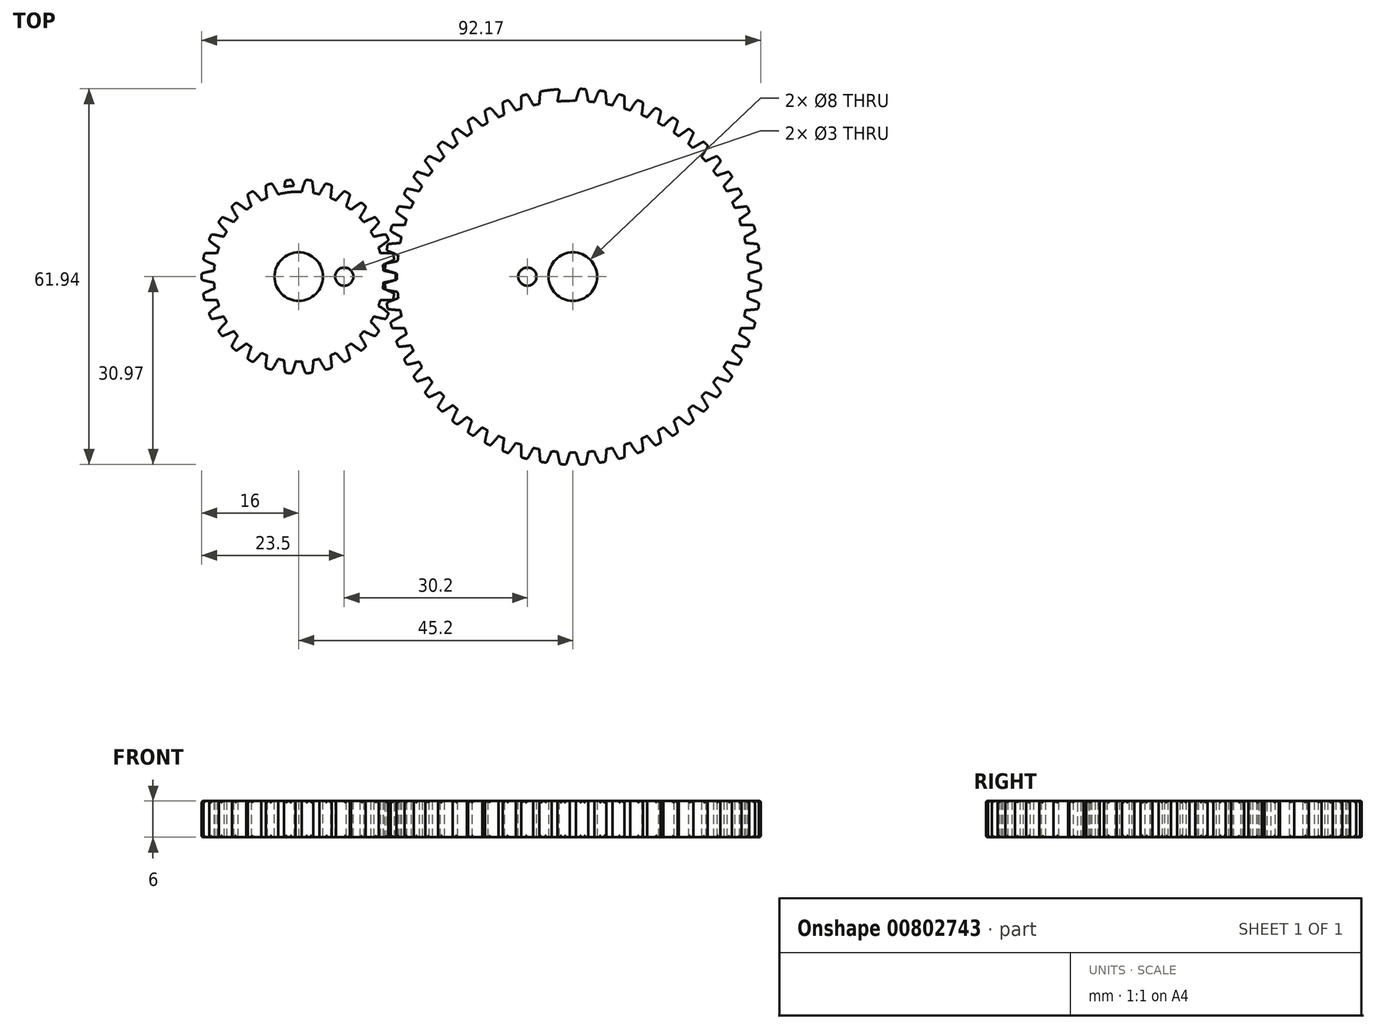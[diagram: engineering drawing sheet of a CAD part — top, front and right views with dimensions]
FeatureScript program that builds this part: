
annotation { "Feature Type Name" : "Feature", "Feature Type Description" : "" }
export const myFeature = defineFeature(function(context is Context, id is Id, definition is map)
    precondition{}
    {
        {
            var Q0;
            Q0=qCreatedBy(makeId("Top.planeOp"),FACE);
            var sketch = newSketch(context, id + "F0", { "sketchPlane" : qUnion([Q0])});
            skCircle(sketch, "E0", {"center": v(0, 0) * mm, "radius": 15 * mm});
            skCircle(sketch, "E1", {"center": v(0, 0) * mm, "radius": 16 * mm});
            skCircle(sketch, "E2", {"center": v(0, 0) * mm, "radius": 14 * mm});
            skLineSegment(sketch, "E3", {"start": v(0, 15) * mm, "end": v(-0.79, 14.98) * mm});
            skLineSegment(sketch, "E4", {"start": v(0, 14) * mm, "end": v(-0.5, 14) * mm});
            skPoint(sketch, "E5.third.point", {"position": v(-19, -4.14) * mm});
            skArc(sketch, "E6.trimOffspring", {"start": v(-0.5, 14) * mm, "mid": v(-0.79, 14.99) * mm, "end": v(-1.14, 15.96) * mm});
            skArc(sketch, "E7.MirrorCS", {"start": v(0.5, 14) * mm, "mid": v(0.79, 14.99) * mm, "end": v(1.14, 15.96) * mm});
            skArc(sketch, "E8.1.0", {"start": v(-3.4, 13.58) * mm, "mid": v(-3.89, 14.5) * mm, "end": v(-4.44, 15.37) * mm});
            skArc(sketch, "E8.1.1", {"start": v(-2.42, 13.79) * mm, "mid": v(-2.35, 14.82) * mm, "end": v(-2.2, 15.85) * mm});
            skArc(sketch, "E8.2.0", {"start": v(-6.15, 12.58) * mm, "mid": v(-6.81, 13.37) * mm, "end": v(-7.54, 14.11) * mm});
            skArc(sketch, "E8.2.1", {"start": v(-5.23, 12.98) * mm, "mid": v(-5.38, 14.01) * mm, "end": v(-5.45, 15.04) * mm});
            skArc(sketch, "E9.1.3.0", {"start": v(-8.63, 11.03) * mm, "mid": v(-9.45, 11.66) * mm, "end": v(-10.3, 12.24) * mm});
            skArc(sketch, "E9.4.3.0", {"start": v(-7.82, 11.61) * mm, "mid": v(-8.17, 12.59) * mm, "end": v(-8.46, 13.58) * mm});
            skArc(sketch, "E9.1.4.0", {"start": v(-10.73, 9) * mm, "mid": v(-11.66, 9.44) * mm, "end": v(-12.62, 9.83) * mm});
            skArc(sketch, "E9.4.4.0", {"start": v(-10.06, 9.73) * mm, "mid": v(-10.61, 10.61) * mm, "end": v(-11.1, 11.53) * mm});
            skArc(sketch, "E9.1.5.0", {"start": v(-12.37, 6.56) * mm, "mid": v(-13.37, 6.81) * mm, "end": v(-14.4, 6.99) * mm});
            skArc(sketch, "E9.4.5.0", {"start": v(-11.87, 7.43) * mm, "mid": v(-12.58, 8.17) * mm, "end": v(-13.25, 8.97) * mm});
            skArc(sketch, "E9.1.6.0", {"start": v(-13.46, 3.85) * mm, "mid": v(-14.5, 3.88) * mm, "end": v(-15.53, 3.84) * mm});
            skArc(sketch, "E9.4.6.0", {"start": v(-13.15, 4.8) * mm, "mid": v(-14, 5.38) * mm, "end": v(-14.82, 6.02) * mm});
            skArc(sketch, "E9.1.7.0", {"start": v(-13.97, 0.97) * mm, "mid": v(-14.99, 0.78) * mm, "end": v(-16, 0.53) * mm});
            skArc(sketch, "E9.4.7.0", {"start": v(-13.86, 1.96) * mm, "mid": v(-14.82, 2.35) * mm, "end": v(-15.75, 2.8) * mm});
            skArc(sketch, "E9.1.8.0", {"start": v(-13.86, -1.96) * mm, "mid": v(-14.82, -2.35) * mm, "end": v(-15.75, -2.8) * mm});
            skArc(sketch, "E9.4.8.0", {"start": v(-13.97, -0.97) * mm, "mid": v(-14.99, -0.78) * mm, "end": v(-16, -0.53) * mm});
            skArc(sketch, "E9.1.9.0", {"start": v(-13.15, -4.8) * mm, "mid": v(-14, -5.38) * mm, "end": v(-14.82, -6.02) * mm});
            skArc(sketch, "E9.4.9.0", {"start": v(-13.46, -3.85) * mm, "mid": v(-14.5, -3.88) * mm, "end": v(-15.53, -3.84) * mm});
            skArc(sketch, "E9.1.10.0", {"start": v(-11.87, -7.43) * mm, "mid": v(-12.58, -8.17) * mm, "end": v(-13.25, -8.97) * mm});
            skArc(sketch, "E9.4.10.0", {"start": v(-12.37, -6.56) * mm, "mid": v(-13.37, -6.81) * mm, "end": v(-14.4, -6.99) * mm});
            skArc(sketch, "E9.1.11.0", {"start": v(-10.06, -9.73) * mm, "mid": v(-10.61, -10.61) * mm, "end": v(-11.1, -11.53) * mm});
            skArc(sketch, "E9.4.11.0", {"start": v(-10.73, -9) * mm, "mid": v(-11.66, -9.44) * mm, "end": v(-12.62, -9.83) * mm});
            skArc(sketch, "E9.1.12.0", {"start": v(-7.82, -11.61) * mm, "mid": v(-8.17, -12.59) * mm, "end": v(-8.46, -13.58) * mm});
            skArc(sketch, "E9.4.12.0", {"start": v(-8.63, -11.03) * mm, "mid": v(-9.45, -11.66) * mm, "end": v(-10.3, -12.24) * mm});
            skArc(sketch, "E9.1.13.0", {"start": v(-5.23, -12.98) * mm, "mid": v(-5.38, -14.01) * mm, "end": v(-5.45, -15.04) * mm});
            skArc(sketch, "E9.4.13.0", {"start": v(-6.15, -12.58) * mm, "mid": v(-6.81, -13.37) * mm, "end": v(-7.54, -14.11) * mm});
            skArc(sketch, "E9.1.14.0", {"start": v(-2.42, -13.79) * mm, "mid": v(-2.35, -14.82) * mm, "end": v(-2.2, -15.85) * mm});
            skArc(sketch, "E9.4.14.0", {"start": v(-3.4, -13.58) * mm, "mid": v(-3.89, -14.5) * mm, "end": v(-4.44, -15.37) * mm});
            skArc(sketch, "E9.1.15.0", {"start": v(0.5, -14) * mm, "mid": v(0.79, -14.99) * mm, "end": v(1.14, -15.96) * mm});
            skArc(sketch, "E9.4.15.0", {"start": v(-0.5, -14) * mm, "mid": v(-0.79, -14.99) * mm, "end": v(-1.14, -15.96) * mm});
            skArc(sketch, "E9.1.16.0", {"start": v(3.4, -13.58) * mm, "mid": v(3.89, -14.5) * mm, "end": v(4.44, -15.37) * mm});
            skArc(sketch, "E9.4.16.0", {"start": v(2.42, -13.79) * mm, "mid": v(2.35, -14.82) * mm, "end": v(2.2, -15.85) * mm});
            skArc(sketch, "E9.1.17.0", {"start": v(6.15, -12.58) * mm, "mid": v(6.81, -13.37) * mm, "end": v(7.54, -14.11) * mm});
            skArc(sketch, "E9.4.17.0", {"start": v(5.23, -12.98) * mm, "mid": v(5.38, -14.01) * mm, "end": v(5.45, -15.04) * mm});
            skArc(sketch, "E9.1.18.0", {"start": v(8.63, -11.03) * mm, "mid": v(9.45, -11.66) * mm, "end": v(10.3, -12.24) * mm});
            skArc(sketch, "E9.4.18.0", {"start": v(7.82, -11.61) * mm, "mid": v(8.17, -12.59) * mm, "end": v(8.46, -13.58) * mm});
            skArc(sketch, "E9.1.19.0", {"start": v(10.73, -9) * mm, "mid": v(11.66, -9.44) * mm, "end": v(12.62, -9.83) * mm});
            skArc(sketch, "E9.4.19.0", {"start": v(10.06, -9.73) * mm, "mid": v(10.61, -10.61) * mm, "end": v(11.1, -11.53) * mm});
            skArc(sketch, "E9.1.20.0", {"start": v(12.37, -6.56) * mm, "mid": v(13.37, -6.81) * mm, "end": v(14.4, -6.99) * mm});
            skArc(sketch, "E9.4.20.0", {"start": v(11.87, -7.43) * mm, "mid": v(12.58, -8.17) * mm, "end": v(13.25, -8.97) * mm});
            skArc(sketch, "E9.1.21.0", {"start": v(13.46, -3.85) * mm, "mid": v(14.5, -3.88) * mm, "end": v(15.53, -3.84) * mm});
            skArc(sketch, "E9.4.21.0", {"start": v(13.15, -4.8) * mm, "mid": v(14, -5.38) * mm, "end": v(14.82, -6.02) * mm});
            skArc(sketch, "E9.1.22.0", {"start": v(13.97, -0.97) * mm, "mid": v(14.99, -0.78) * mm, "end": v(16, -0.53) * mm});
            skArc(sketch, "E9.4.22.0", {"start": v(13.86, -1.96) * mm, "mid": v(14.82, -2.35) * mm, "end": v(15.75, -2.8) * mm});
            skArc(sketch, "E9.1.23.0", {"start": v(13.86, 1.96) * mm, "mid": v(14.82, 2.35) * mm, "end": v(15.75, 2.8) * mm});
            skArc(sketch, "E9.4.23.0", {"start": v(13.97, 0.97) * mm, "mid": v(14.99, 0.78) * mm, "end": v(16, 0.53) * mm});
            skArc(sketch, "E9.1.24.0", {"start": v(13.15, 4.8) * mm, "mid": v(14, 5.38) * mm, "end": v(14.82, 6.02) * mm});
            skArc(sketch, "E9.4.24.0", {"start": v(13.46, 3.85) * mm, "mid": v(14.5, 3.88) * mm, "end": v(15.53, 3.84) * mm});
            skArc(sketch, "E9.1.25.0", {"start": v(11.87, 7.43) * mm, "mid": v(12.58, 8.17) * mm, "end": v(13.25, 8.97) * mm});
            skArc(sketch, "E9.4.25.0", {"start": v(12.37, 6.56) * mm, "mid": v(13.37, 6.81) * mm, "end": v(14.4, 6.99) * mm});
            skArc(sketch, "E9.1.26.0", {"start": v(10.06, 9.73) * mm, "mid": v(10.61, 10.61) * mm, "end": v(11.1, 11.53) * mm});
            skArc(sketch, "E9.4.26.0", {"start": v(10.73, 9) * mm, "mid": v(11.66, 9.44) * mm, "end": v(12.62, 9.83) * mm});
            skArc(sketch, "E9.1.27.0", {"start": v(7.82, 11.61) * mm, "mid": v(8.17, 12.59) * mm, "end": v(8.46, 13.58) * mm});
            skArc(sketch, "E9.4.27.0", {"start": v(8.63, 11.03) * mm, "mid": v(9.45, 11.66) * mm, "end": v(10.3, 12.24) * mm});
            skArc(sketch, "E9.1.28.0", {"start": v(5.23, 12.98) * mm, "mid": v(5.38, 14.01) * mm, "end": v(5.45, 15.04) * mm});
            skArc(sketch, "E9.4.28.0", {"start": v(6.15, 12.58) * mm, "mid": v(6.81, 13.37) * mm, "end": v(7.54, 14.11) * mm});
            skArc(sketch, "E9.1.29.0", {"start": v(2.42, 13.79) * mm, "mid": v(2.35, 14.82) * mm, "end": v(2.2, 15.85) * mm});
            skArc(sketch, "E9.4.29.0", {"start": v(3.4, 13.58) * mm, "mid": v(3.89, 14.5) * mm, "end": v(4.44, 15.37) * mm});
            skSolve(sketch);
        }
        {
            var Q0;
            {var subQ0=sQuery(id+"F0.wireOp",EDGE,"E9.1.14.0");var subQ1=sQuery(id+"F0.wireOp",EDGE,"E0");var subQ2=makeQuery(id+"F0.imprint","INTERSECT",VERTEX,{"derivedFrom":[subQ1,subQ0]});Q0=makeQuery(id+"F0.imprint","IMPRINT",FACE,{"disambiguationData":[TD([[makeQuery(id+"F0.imprint","IMPRINT",EDGE,{"disambiguationData":[TD([[subQ2,-1.0]])],"derivedFrom":subQ1}),-1.0]])]});}
            var Q1;
            {var subQ0=sQuery(id+"F0.wireOp",EDGE,"E9.4.23.0");var subQ1=sQuery(id+"F0.wireOp",EDGE,"E0");var subQ2=makeQuery(id+"F0.imprint","INTERSECT",VERTEX,{"derivedFrom":[subQ1,subQ0]});Q1=makeQuery(id+"F0.imprint","IMPRINT",FACE,{"disambiguationData":[TD([[makeQuery(id+"F0.imprint","IMPRINT",EDGE,{"disambiguationData":[TD([[subQ2,1.0]])],"derivedFrom":subQ1}),-1.0]])]});}
            var Q2;
            {var subQ0=sQuery(id+"F0.wireOp",EDGE,"E9.1.11.0");var subQ1=sQuery(id+"F0.wireOp",EDGE,"E0");var subQ2=makeQuery(id+"F0.imprint","INTERSECT",VERTEX,{"derivedFrom":[subQ1,subQ0]});Q2=makeQuery(id+"F0.imprint","IMPRINT",FACE,{"disambiguationData":[TD([[makeQuery(id+"F0.imprint","IMPRINT",EDGE,{"disambiguationData":[TD([[subQ2,-1.0]])],"derivedFrom":subQ1}),-1.0]])]});}
            var Q3;
            {var subQ0=sQuery(id+"F0.wireOp",EDGE,"E9.1.21.0");var subQ1=sQuery(id+"F0.wireOp",EDGE,"E0");var subQ2=makeQuery(id+"F0.imprint","INTERSECT",VERTEX,{"derivedFrom":[subQ1,subQ0]});Q3=makeQuery(id+"F0.imprint","IMPRINT",FACE,{"disambiguationData":[TD([[makeQuery(id+"F0.imprint","IMPRINT",EDGE,{"disambiguationData":[TD([[subQ2,-1.0]])],"derivedFrom":subQ1}),-1.0]])]});}
            var Q4;
            {var subQ0=sQuery(id+"F0.wireOp",EDGE,"E9.1.10.0");var subQ1=sQuery(id+"F0.wireOp",EDGE,"E0");var subQ2=makeQuery(id+"F0.imprint","INTERSECT",VERTEX,{"derivedFrom":[subQ1,subQ0]});Q4=makeQuery(id+"F0.imprint","IMPRINT",FACE,{"disambiguationData":[TD([[makeQuery(id+"F0.imprint","IMPRINT",EDGE,{"disambiguationData":[TD([[subQ2,-1.0]])],"derivedFrom":subQ1}),-1.0]])]});}
            var Q5;
            {var subQ0=sQuery(id+"F0.wireOp",EDGE,"E9.1.7.0");var subQ1=sQuery(id+"F0.wireOp",EDGE,"E0");var subQ2=makeQuery(id+"F0.imprint","INTERSECT",VERTEX,{"derivedFrom":[subQ1,subQ0]});Q5=makeQuery(id+"F0.imprint","IMPRINT",FACE,{"disambiguationData":[TD([[makeQuery(id+"F0.imprint","IMPRINT",EDGE,{"disambiguationData":[TD([[subQ2,-1.0]])],"derivedFrom":subQ1}),-1.0]])]});}
            var Q6;
            {var subQ0=sQuery(id+"F0.wireOp",EDGE,"E8.1.0");var subQ1=sQuery(id+"F0.wireOp",EDGE,"E0");var subQ2=makeQuery(id+"F0.imprint","INTERSECT",VERTEX,{"derivedFrom":[subQ1,subQ0]});Q6=makeQuery(id+"F0.imprint","IMPRINT",FACE,{"disambiguationData":[TD([[makeQuery(id+"F0.imprint","IMPRINT",EDGE,{"disambiguationData":[TD([[subQ2,-1.0]])],"derivedFrom":subQ1}),-1.0]])]});}
            var Q7;
            {var subQ0=sQuery(id+"F0.wireOp",EDGE,"E9.1.13.0");var subQ1=sQuery(id+"F0.wireOp",EDGE,"E0");var subQ2=makeQuery(id+"F0.imprint","INTERSECT",VERTEX,{"derivedFrom":[subQ1,subQ0]});Q7=makeQuery(id+"F0.imprint","IMPRINT",FACE,{"disambiguationData":[TD([[makeQuery(id+"F0.imprint","IMPRINT",EDGE,{"disambiguationData":[TD([[subQ2,-1.0]])],"derivedFrom":subQ1}),-1.0]])]});}
            var Q8;
            {var subQ0=sQuery(id+"F0.wireOp",EDGE,"E9.1.9.0");var subQ1=sQuery(id+"F0.wireOp",EDGE,"E0");var subQ2=makeQuery(id+"F0.imprint","INTERSECT",VERTEX,{"derivedFrom":[subQ1,subQ0]});Q8=makeQuery(id+"F0.imprint","IMPRINT",FACE,{"disambiguationData":[TD([[makeQuery(id+"F0.imprint","IMPRINT",EDGE,{"disambiguationData":[TD([[subQ2,-1.0]])],"derivedFrom":subQ1}),-1.0]])]});}
            var Q9;
            {var subQ0=sQuery(id+"F0.wireOp",EDGE,"E9.1.18.0");var subQ1=sQuery(id+"F0.wireOp",EDGE,"E0");var subQ2=makeQuery(id+"F0.imprint","INTERSECT",VERTEX,{"derivedFrom":[subQ1,subQ0]});Q9=makeQuery(id+"F0.imprint","IMPRINT",FACE,{"disambiguationData":[TD([[makeQuery(id+"F0.imprint","IMPRINT",EDGE,{"disambiguationData":[TD([[subQ2,-1.0]])],"derivedFrom":subQ1}),-1.0]])]});}
            var Q10;
            {var subQ0=sQuery(id+"F0.wireOp",EDGE,"E9.1.17.0");var subQ1=sQuery(id+"F0.wireOp",EDGE,"E0");var subQ2=makeQuery(id+"F0.imprint","INTERSECT",VERTEX,{"derivedFrom":[subQ1,subQ0]});Q10=makeQuery(id+"F0.imprint","IMPRINT",FACE,{"disambiguationData":[TD([[makeQuery(id+"F0.imprint","IMPRINT",EDGE,{"disambiguationData":[TD([[subQ2,-1.0]])],"derivedFrom":subQ1}),-1.0]])]});}
            var Q11;
            {var subQ0=sQuery(id+"F0.wireOp",EDGE,"E9.1.5.0");var subQ1=sQuery(id+"F0.wireOp",EDGE,"E0");var subQ2=makeQuery(id+"F0.imprint","INTERSECT",VERTEX,{"derivedFrom":[subQ1,subQ0]});Q11=makeQuery(id+"F0.imprint","IMPRINT",FACE,{"disambiguationData":[TD([[makeQuery(id+"F0.imprint","IMPRINT",EDGE,{"disambiguationData":[TD([[subQ2,-1.0]])],"derivedFrom":subQ1}),-1.0]])]});}
            var Q12;
            {var subQ0=sQuery(id+"F0.wireOp",EDGE,"E8.2.0");var subQ1=sQuery(id+"F0.wireOp",EDGE,"E0");var subQ2=makeQuery(id+"F0.imprint","INTERSECT",VERTEX,{"derivedFrom":[subQ1,subQ0]});Q12=makeQuery(id+"F0.imprint","IMPRINT",FACE,{"disambiguationData":[TD([[makeQuery(id+"F0.imprint","IMPRINT",EDGE,{"disambiguationData":[TD([[subQ2,-1.0]])],"derivedFrom":subQ1}),-1.0]])]});}
            var Q13;
            {var subQ0=sQuery(id+"F0.wireOp",EDGE,"E9.1.28.0");var subQ1=sQuery(id+"F0.wireOp",EDGE,"E0");var subQ2=makeQuery(id+"F0.imprint","INTERSECT",VERTEX,{"derivedFrom":[subQ1,subQ0]});Q13=makeQuery(id+"F0.imprint","IMPRINT",FACE,{"disambiguationData":[TD([[makeQuery(id+"F0.imprint","IMPRINT",EDGE,{"disambiguationData":[TD([[subQ2,-1.0]])],"derivedFrom":subQ1}),-1.0]])]});}
            var Q14;
            {var subQ0=sQuery(id+"F0.wireOp",EDGE,"E9.1.29.0");var subQ1=sQuery(id+"F0.wireOp",EDGE,"E0");var subQ2=makeQuery(id+"F0.imprint","INTERSECT",VERTEX,{"derivedFrom":[subQ1,subQ0]});Q14=makeQuery(id+"F0.imprint","IMPRINT",FACE,{"disambiguationData":[TD([[makeQuery(id+"F0.imprint","IMPRINT",EDGE,{"disambiguationData":[TD([[subQ2,-1.0]])],"derivedFrom":subQ1}),-1.0]])]});}
            var Q15;
            {var subQ0=sQuery(id+"F0.wireOp",EDGE,"E9.1.24.0");var subQ1=sQuery(id+"F0.wireOp",EDGE,"E0");var subQ2=makeQuery(id+"F0.imprint","INTERSECT",VERTEX,{"derivedFrom":[subQ1,subQ0]});Q15=makeQuery(id+"F0.imprint","IMPRINT",FACE,{"disambiguationData":[TD([[makeQuery(id+"F0.imprint","IMPRINT",EDGE,{"disambiguationData":[TD([[subQ2,-1.0]])],"derivedFrom":subQ1}),-1.0]])]});}
            var Q16;
            {var subQ0=sQuery(id+"F0.wireOp",EDGE,"E6.trimOffspring");var subQ5=sQuery(id+"F0.wireOp",EDGE,"E1");var subQ6=makeQuery(id+"F0.imprint","INTERSECT",VERTEX,{"derivedFrom":[subQ5,subQ0]});Q16=makeQuery(id+"F0.imprint","IMPRINT",FACE,{"disambiguationData":[TD([[makeQuery(id+"F0.imprint","IMPRINT",EDGE,{"disambiguationData":[TD([[subQ6,-1.0]])],"derivedFrom":subQ5}),1.0]])]});}
            var Q17;
            {var subQ0=sQuery(id+"F0.wireOp",EDGE,"E9.1.27.0");var subQ1=sQuery(id+"F0.wireOp",EDGE,"E0");var subQ2=makeQuery(id+"F0.imprint","INTERSECT",VERTEX,{"derivedFrom":[subQ1,subQ0]});Q17=makeQuery(id+"F0.imprint","IMPRINT",FACE,{"disambiguationData":[TD([[makeQuery(id+"F0.imprint","IMPRINT",EDGE,{"disambiguationData":[TD([[subQ2,-1.0]])],"derivedFrom":subQ1}),-1.0]])]});}
            var Q18;
            {var subQ0=sQuery(id+"F0.wireOp",EDGE,"E9.1.6.0");var subQ1=sQuery(id+"F0.wireOp",EDGE,"E0");var subQ2=makeQuery(id+"F0.imprint","INTERSECT",VERTEX,{"derivedFrom":[subQ1,subQ0]});Q18=makeQuery(id+"F0.imprint","IMPRINT",FACE,{"disambiguationData":[TD([[makeQuery(id+"F0.imprint","IMPRINT",EDGE,{"disambiguationData":[TD([[subQ2,-1.0]])],"derivedFrom":subQ1}),-1.0]])]});}
            var Q19;
            {var subQ0=sQuery(id+"F0.wireOp",EDGE,"E9.1.16.0");var subQ1=sQuery(id+"F0.wireOp",EDGE,"E0");var subQ2=makeQuery(id+"F0.imprint","INTERSECT",VERTEX,{"derivedFrom":[subQ1,subQ0]});Q19=makeQuery(id+"F0.imprint","IMPRINT",FACE,{"disambiguationData":[TD([[makeQuery(id+"F0.imprint","IMPRINT",EDGE,{"disambiguationData":[TD([[subQ2,-1.0]])],"derivedFrom":subQ1}),-1.0]])]});}
            var Q20;
            {var subQ0=sQuery(id+"F0.wireOp",EDGE,"E9.1.12.0");var subQ1=sQuery(id+"F0.wireOp",EDGE,"E0");var subQ2=makeQuery(id+"F0.imprint","INTERSECT",VERTEX,{"derivedFrom":[subQ1,subQ0]});Q20=makeQuery(id+"F0.imprint","IMPRINT",FACE,{"disambiguationData":[TD([[makeQuery(id+"F0.imprint","IMPRINT",EDGE,{"disambiguationData":[TD([[subQ2,-1.0]])],"derivedFrom":subQ1}),-1.0]])]});}
            var Q21;
            {var subQ0=sQuery(id+"F0.wireOp",EDGE,"E9.1.20.0");var subQ1=sQuery(id+"F0.wireOp",EDGE,"E0");var subQ2=makeQuery(id+"F0.imprint","INTERSECT",VERTEX,{"derivedFrom":[subQ1,subQ0]});Q21=makeQuery(id+"F0.imprint","IMPRINT",FACE,{"disambiguationData":[TD([[makeQuery(id+"F0.imprint","IMPRINT",EDGE,{"disambiguationData":[TD([[subQ2,-1.0]])],"derivedFrom":subQ1}),-1.0]])]});}
            var Q22;
            {var subQ0=sQuery(id+"F0.wireOp",EDGE,"E9.1.4.0");var subQ1=sQuery(id+"F0.wireOp",EDGE,"E0");var subQ2=makeQuery(id+"F0.imprint","INTERSECT",VERTEX,{"derivedFrom":[subQ1,subQ0]});Q22=makeQuery(id+"F0.imprint","IMPRINT",FACE,{"disambiguationData":[TD([[makeQuery(id+"F0.imprint","IMPRINT",EDGE,{"disambiguationData":[TD([[subQ2,-1.0]])],"derivedFrom":subQ1}),-1.0]])]});}
            var Q23;
            {var subQ0=sQuery(id+"F0.wireOp",EDGE,"E9.1.15.0");var subQ1=sQuery(id+"F0.wireOp",EDGE,"E0");var subQ2=makeQuery(id+"F0.imprint","INTERSECT",VERTEX,{"derivedFrom":[subQ1,subQ0]});Q23=makeQuery(id+"F0.imprint","IMPRINT",FACE,{"disambiguationData":[TD([[makeQuery(id+"F0.imprint","IMPRINT",EDGE,{"disambiguationData":[TD([[subQ2,-1.0]])],"derivedFrom":subQ1}),-1.0]])]});}
            var Q24;
            {var subQ0=sQuery(id+"F0.wireOp",EDGE,"E9.1.25.0");var subQ1=sQuery(id+"F0.wireOp",EDGE,"E0");var subQ2=makeQuery(id+"F0.imprint","INTERSECT",VERTEX,{"derivedFrom":[subQ1,subQ0]});Q24=makeQuery(id+"F0.imprint","IMPRINT",FACE,{"disambiguationData":[TD([[makeQuery(id+"F0.imprint","IMPRINT",EDGE,{"disambiguationData":[TD([[subQ2,-1.0]])],"derivedFrom":subQ1}),-1.0]])]});}
            var Q25;
            {var subQ0=sQuery(id+"F0.wireOp",EDGE,"E9.1.19.0");var subQ1=sQuery(id+"F0.wireOp",EDGE,"E0");var subQ2=makeQuery(id+"F0.imprint","INTERSECT",VERTEX,{"derivedFrom":[subQ1,subQ0]});Q25=makeQuery(id+"F0.imprint","IMPRINT",FACE,{"disambiguationData":[TD([[makeQuery(id+"F0.imprint","IMPRINT",EDGE,{"disambiguationData":[TD([[subQ2,-1.0]])],"derivedFrom":subQ1}),-1.0]])]});}
            var Q26;
            {var subQ0=sQuery(id+"F0.wireOp",EDGE,"E9.1.26.0");var subQ1=sQuery(id+"F0.wireOp",EDGE,"E0");var subQ2=makeQuery(id+"F0.imprint","INTERSECT",VERTEX,{"derivedFrom":[subQ1,subQ0]});Q26=makeQuery(id+"F0.imprint","IMPRINT",FACE,{"disambiguationData":[TD([[makeQuery(id+"F0.imprint","IMPRINT",EDGE,{"disambiguationData":[TD([[subQ2,-1.0]])],"derivedFrom":subQ1}),-1.0]])]});}
            var Q27;
            {var subQ0=sQuery(id+"F0.wireOp",EDGE,"E9.1.3.0");var subQ1=sQuery(id+"F0.wireOp",EDGE,"E0");var subQ2=makeQuery(id+"F0.imprint","INTERSECT",VERTEX,{"derivedFrom":[subQ1,subQ0]});Q27=makeQuery(id+"F0.imprint","IMPRINT",FACE,{"disambiguationData":[TD([[makeQuery(id+"F0.imprint","IMPRINT",EDGE,{"disambiguationData":[TD([[subQ2,-1.0]])],"derivedFrom":subQ1}),-1.0]])]});}
            var Q28;
            {var subQ0=sQuery(id+"F0.wireOp",EDGE,"E9.1.23.0");var subQ1=sQuery(id+"F0.wireOp",EDGE,"E0");var subQ2=makeQuery(id+"F0.imprint","INTERSECT",VERTEX,{"derivedFrom":[subQ1,subQ0]});Q28=makeQuery(id+"F0.imprint","IMPRINT",FACE,{"disambiguationData":[TD([[makeQuery(id+"F0.imprint","IMPRINT",EDGE,{"disambiguationData":[TD([[subQ2,-1.0]])],"derivedFrom":subQ1}),-1.0]])]});}
            var Q29;
            {var subQ0=sQuery(id+"F0.wireOp",EDGE,"E9.1.8.0");var subQ1=sQuery(id+"F0.wireOp",EDGE,"E0");var subQ2=makeQuery(id+"F0.imprint","INTERSECT",VERTEX,{"derivedFrom":[subQ1,subQ0]});Q29=makeQuery(id+"F0.imprint","IMPRINT",FACE,{"disambiguationData":[TD([[makeQuery(id+"F0.imprint","IMPRINT",EDGE,{"disambiguationData":[TD([[subQ2,-1.0]])],"derivedFrom":subQ1}),-1.0]])]});}
            var Q30;
            {var subQ41=sQuery(id+"F0.wireOp",EDGE,"E4");Q30=makeQuery(id+"F0.imprint","IMPRINT",FACE,{"disambiguationData":[TD([[makeQuery(id+"F0.imprint","IMPRINT",EDGE,{"derivedFrom":subQ41}),1.0]])]});}
            var Q31;
            {var subQ0=sQuery(id+"F0.wireOp",EDGE,"E9.1.27.0");var subQ1=sQuery(id+"F0.wireOp",EDGE,"E0");var subQ2=makeQuery(id+"F0.imprint","INTERSECT",VERTEX,{"derivedFrom":[subQ1,subQ0]});Q31=makeQuery(id+"F0.imprint","IMPRINT",FACE,{"disambiguationData":[TD([[makeQuery(id+"F0.imprint","IMPRINT",EDGE,{"disambiguationData":[TD([[subQ2,-1.0]])],"derivedFrom":subQ1}),1.0]])]});}
            var Q32;
            {var subQ0=sQuery(id+"F0.wireOp",EDGE,"E9.1.28.0");var subQ1=sQuery(id+"F0.wireOp",EDGE,"E0");var subQ2=makeQuery(id+"F0.imprint","INTERSECT",VERTEX,{"derivedFrom":[subQ1,subQ0]});Q32=makeQuery(id+"F0.imprint","IMPRINT",FACE,{"disambiguationData":[TD([[makeQuery(id+"F0.imprint","IMPRINT",EDGE,{"disambiguationData":[TD([[subQ2,-1.0]])],"derivedFrom":subQ1}),1.0]])]});}
            var Q33;
            {var subQ0=sQuery(id+"F0.wireOp",EDGE,"E9.1.26.0");var subQ1=sQuery(id+"F0.wireOp",EDGE,"E0");var subQ2=makeQuery(id+"F0.imprint","INTERSECT",VERTEX,{"derivedFrom":[subQ1,subQ0]});Q33=makeQuery(id+"F0.imprint","IMPRINT",FACE,{"disambiguationData":[TD([[makeQuery(id+"F0.imprint","IMPRINT",EDGE,{"disambiguationData":[TD([[subQ2,-1.0]])],"derivedFrom":subQ1}),1.0]])]});}
            var Q34;
            {var subQ0=sQuery(id+"F0.wireOp",EDGE,"E9.1.25.0");var subQ1=sQuery(id+"F0.wireOp",EDGE,"E0");var subQ2=makeQuery(id+"F0.imprint","INTERSECT",VERTEX,{"derivedFrom":[subQ1,subQ0]});Q34=makeQuery(id+"F0.imprint","IMPRINT",FACE,{"disambiguationData":[TD([[makeQuery(id+"F0.imprint","IMPRINT",EDGE,{"disambiguationData":[TD([[subQ2,-1.0]])],"derivedFrom":subQ1}),1.0]])]});}
            var Q35;
            {var subQ0=sQuery(id+"F0.wireOp",EDGE,"E9.1.24.0");var subQ1=sQuery(id+"F0.wireOp",EDGE,"E0");var subQ2=makeQuery(id+"F0.imprint","INTERSECT",VERTEX,{"derivedFrom":[subQ1,subQ0]});Q35=makeQuery(id+"F0.imprint","IMPRINT",FACE,{"disambiguationData":[TD([[makeQuery(id+"F0.imprint","IMPRINT",EDGE,{"disambiguationData":[TD([[subQ2,-1.0]])],"derivedFrom":subQ1}),1.0]])]});}
            var Q36;
            {var subQ0=sQuery(id+"F0.wireOp",EDGE,"E9.1.23.0");var subQ1=sQuery(id+"F0.wireOp",EDGE,"E0");var subQ2=makeQuery(id+"F0.imprint","INTERSECT",VERTEX,{"derivedFrom":[subQ1,subQ0]});Q36=makeQuery(id+"F0.imprint","IMPRINT",FACE,{"disambiguationData":[TD([[makeQuery(id+"F0.imprint","IMPRINT",EDGE,{"disambiguationData":[TD([[subQ2,-1.0]])],"derivedFrom":subQ1}),1.0]])]});}
            var Q37;
            {var subQ0=sQuery(id+"F0.wireOp",EDGE,"E9.4.23.0");var subQ1=sQuery(id+"F0.wireOp",EDGE,"E0");var subQ2=makeQuery(id+"F0.imprint","INTERSECT",VERTEX,{"derivedFrom":[subQ1,subQ0]});Q37=makeQuery(id+"F0.imprint","IMPRINT",FACE,{"disambiguationData":[TD([[makeQuery(id+"F0.imprint","IMPRINT",EDGE,{"disambiguationData":[TD([[subQ2,1.0]])],"derivedFrom":subQ1}),1.0]])]});}
            var Q38;
            {var subQ0=sQuery(id+"F0.wireOp",EDGE,"E9.1.21.0");var subQ1=sQuery(id+"F0.wireOp",EDGE,"E0");var subQ2=makeQuery(id+"F0.imprint","INTERSECT",VERTEX,{"derivedFrom":[subQ1,subQ0]});Q38=makeQuery(id+"F0.imprint","IMPRINT",FACE,{"disambiguationData":[TD([[makeQuery(id+"F0.imprint","IMPRINT",EDGE,{"disambiguationData":[TD([[subQ2,-1.0]])],"derivedFrom":subQ1}),1.0]])]});}
            var Q39;
            {var subQ0=sQuery(id+"F0.wireOp",EDGE,"E9.1.20.0");var subQ1=sQuery(id+"F0.wireOp",EDGE,"E0");var subQ2=makeQuery(id+"F0.imprint","INTERSECT",VERTEX,{"derivedFrom":[subQ1,subQ0]});Q39=makeQuery(id+"F0.imprint","IMPRINT",FACE,{"disambiguationData":[TD([[makeQuery(id+"F0.imprint","IMPRINT",EDGE,{"disambiguationData":[TD([[subQ2,-1.0]])],"derivedFrom":subQ1}),1.0]])]});}
            var Q40;
            {var subQ0=sQuery(id+"F0.wireOp",EDGE,"E9.1.19.0");var subQ1=sQuery(id+"F0.wireOp",EDGE,"E0");var subQ2=makeQuery(id+"F0.imprint","INTERSECT",VERTEX,{"derivedFrom":[subQ1,subQ0]});Q40=makeQuery(id+"F0.imprint","IMPRINT",FACE,{"disambiguationData":[TD([[makeQuery(id+"F0.imprint","IMPRINT",EDGE,{"disambiguationData":[TD([[subQ2,-1.0]])],"derivedFrom":subQ1}),1.0]])]});}
            var Q41;
            {var subQ0=sQuery(id+"F0.wireOp",EDGE,"E9.1.18.0");var subQ1=sQuery(id+"F0.wireOp",EDGE,"E0");var subQ2=makeQuery(id+"F0.imprint","INTERSECT",VERTEX,{"derivedFrom":[subQ1,subQ0]});Q41=makeQuery(id+"F0.imprint","IMPRINT",FACE,{"disambiguationData":[TD([[makeQuery(id+"F0.imprint","IMPRINT",EDGE,{"disambiguationData":[TD([[subQ2,-1.0]])],"derivedFrom":subQ1}),1.0]])]});}
            var Q42;
            {var subQ0=sQuery(id+"F0.wireOp",EDGE,"E9.1.17.0");var subQ1=sQuery(id+"F0.wireOp",EDGE,"E0");var subQ2=makeQuery(id+"F0.imprint","INTERSECT",VERTEX,{"derivedFrom":[subQ1,subQ0]});Q42=makeQuery(id+"F0.imprint","IMPRINT",FACE,{"disambiguationData":[TD([[makeQuery(id+"F0.imprint","IMPRINT",EDGE,{"disambiguationData":[TD([[subQ2,-1.0]])],"derivedFrom":subQ1}),1.0]])]});}
            var Q43;
            {var subQ0=sQuery(id+"F0.wireOp",EDGE,"E9.1.16.0");var subQ1=sQuery(id+"F0.wireOp",EDGE,"E0");var subQ2=makeQuery(id+"F0.imprint","INTERSECT",VERTEX,{"derivedFrom":[subQ1,subQ0]});Q43=makeQuery(id+"F0.imprint","IMPRINT",FACE,{"disambiguationData":[TD([[makeQuery(id+"F0.imprint","IMPRINT",EDGE,{"disambiguationData":[TD([[subQ2,-1.0]])],"derivedFrom":subQ1}),1.0]])]});}
            var Q44;
            {var subQ0=sQuery(id+"F0.wireOp",EDGE,"E9.1.15.0");var subQ1=sQuery(id+"F0.wireOp",EDGE,"E0");var subQ2=makeQuery(id+"F0.imprint","INTERSECT",VERTEX,{"derivedFrom":[subQ1,subQ0]});Q44=makeQuery(id+"F0.imprint","IMPRINT",FACE,{"disambiguationData":[TD([[makeQuery(id+"F0.imprint","IMPRINT",EDGE,{"disambiguationData":[TD([[subQ2,-1.0]])],"derivedFrom":subQ1}),1.0]])]});}
            var Q45;
            {var subQ0=sQuery(id+"F0.wireOp",EDGE,"E9.1.14.0");var subQ1=sQuery(id+"F0.wireOp",EDGE,"E0");var subQ2=makeQuery(id+"F0.imprint","INTERSECT",VERTEX,{"derivedFrom":[subQ1,subQ0]});Q45=makeQuery(id+"F0.imprint","IMPRINT",FACE,{"disambiguationData":[TD([[makeQuery(id+"F0.imprint","IMPRINT",EDGE,{"disambiguationData":[TD([[subQ2,-1.0]])],"derivedFrom":subQ1}),1.0]])]});}
            var Q46;
            {var subQ0=sQuery(id+"F0.wireOp",EDGE,"E9.1.13.0");var subQ1=sQuery(id+"F0.wireOp",EDGE,"E0");var subQ2=makeQuery(id+"F0.imprint","INTERSECT",VERTEX,{"derivedFrom":[subQ1,subQ0]});Q46=makeQuery(id+"F0.imprint","IMPRINT",FACE,{"disambiguationData":[TD([[makeQuery(id+"F0.imprint","IMPRINT",EDGE,{"disambiguationData":[TD([[subQ2,-1.0]])],"derivedFrom":subQ1}),1.0]])]});}
            var Q47;
            {var subQ0=sQuery(id+"F0.wireOp",EDGE,"E9.1.12.0");var subQ1=sQuery(id+"F0.wireOp",EDGE,"E0");var subQ2=makeQuery(id+"F0.imprint","INTERSECT",VERTEX,{"derivedFrom":[subQ1,subQ0]});Q47=makeQuery(id+"F0.imprint","IMPRINT",FACE,{"disambiguationData":[TD([[makeQuery(id+"F0.imprint","IMPRINT",EDGE,{"disambiguationData":[TD([[subQ2,-1.0]])],"derivedFrom":subQ1}),1.0]])]});}
            var Q48;
            {var subQ0=sQuery(id+"F0.wireOp",EDGE,"E9.1.11.0");var subQ1=sQuery(id+"F0.wireOp",EDGE,"E0");var subQ2=makeQuery(id+"F0.imprint","INTERSECT",VERTEX,{"derivedFrom":[subQ1,subQ0]});Q48=makeQuery(id+"F0.imprint","IMPRINT",FACE,{"disambiguationData":[TD([[makeQuery(id+"F0.imprint","IMPRINT",EDGE,{"disambiguationData":[TD([[subQ2,-1.0]])],"derivedFrom":subQ1}),1.0]])]});}
            var Q49;
            {var subQ0=sQuery(id+"F0.wireOp",EDGE,"E9.1.10.0");var subQ1=sQuery(id+"F0.wireOp",EDGE,"E0");var subQ2=makeQuery(id+"F0.imprint","INTERSECT",VERTEX,{"derivedFrom":[subQ1,subQ0]});Q49=makeQuery(id+"F0.imprint","IMPRINT",FACE,{"disambiguationData":[TD([[makeQuery(id+"F0.imprint","IMPRINT",EDGE,{"disambiguationData":[TD([[subQ2,-1.0]])],"derivedFrom":subQ1}),1.0]])]});}
            var Q50;
            {var subQ0=sQuery(id+"F0.wireOp",EDGE,"E9.1.9.0");var subQ1=sQuery(id+"F0.wireOp",EDGE,"E0");var subQ2=makeQuery(id+"F0.imprint","INTERSECT",VERTEX,{"derivedFrom":[subQ1,subQ0]});Q50=makeQuery(id+"F0.imprint","IMPRINT",FACE,{"disambiguationData":[TD([[makeQuery(id+"F0.imprint","IMPRINT",EDGE,{"disambiguationData":[TD([[subQ2,-1.0]])],"derivedFrom":subQ1}),1.0]])]});}
            var Q51;
            {var subQ0=sQuery(id+"F0.wireOp",EDGE,"E9.1.8.0");var subQ1=sQuery(id+"F0.wireOp",EDGE,"E0");var subQ2=makeQuery(id+"F0.imprint","INTERSECT",VERTEX,{"derivedFrom":[subQ1,subQ0]});Q51=makeQuery(id+"F0.imprint","IMPRINT",FACE,{"disambiguationData":[TD([[makeQuery(id+"F0.imprint","IMPRINT",EDGE,{"disambiguationData":[TD([[subQ2,-1.0]])],"derivedFrom":subQ1}),1.0]])]});}
            var Q52;
            {var subQ0=sQuery(id+"F0.wireOp",EDGE,"E9.1.7.0");var subQ1=sQuery(id+"F0.wireOp",EDGE,"E0");var subQ2=makeQuery(id+"F0.imprint","INTERSECT",VERTEX,{"derivedFrom":[subQ1,subQ0]});Q52=makeQuery(id+"F0.imprint","IMPRINT",FACE,{"disambiguationData":[TD([[makeQuery(id+"F0.imprint","IMPRINT",EDGE,{"disambiguationData":[TD([[subQ2,-1.0]])],"derivedFrom":subQ1}),1.0]])]});}
            var Q53;
            {var subQ0=sQuery(id+"F0.wireOp",EDGE,"E9.1.6.0");var subQ1=sQuery(id+"F0.wireOp",EDGE,"E0");var subQ2=makeQuery(id+"F0.imprint","INTERSECT",VERTEX,{"derivedFrom":[subQ1,subQ0]});Q53=makeQuery(id+"F0.imprint","IMPRINT",FACE,{"disambiguationData":[TD([[makeQuery(id+"F0.imprint","IMPRINT",EDGE,{"disambiguationData":[TD([[subQ2,-1.0]])],"derivedFrom":subQ1}),1.0]])]});}
            var Q54;
            {var subQ0=sQuery(id+"F0.wireOp",EDGE,"E9.1.5.0");var subQ1=sQuery(id+"F0.wireOp",EDGE,"E0");var subQ2=makeQuery(id+"F0.imprint","INTERSECT",VERTEX,{"derivedFrom":[subQ1,subQ0]});Q54=makeQuery(id+"F0.imprint","IMPRINT",FACE,{"disambiguationData":[TD([[makeQuery(id+"F0.imprint","IMPRINT",EDGE,{"disambiguationData":[TD([[subQ2,-1.0]])],"derivedFrom":subQ1}),1.0]])]});}
            var Q55;
            {var subQ0=sQuery(id+"F0.wireOp",EDGE,"E9.1.4.0");var subQ1=sQuery(id+"F0.wireOp",EDGE,"E0");var subQ2=makeQuery(id+"F0.imprint","INTERSECT",VERTEX,{"derivedFrom":[subQ1,subQ0]});Q55=makeQuery(id+"F0.imprint","IMPRINT",FACE,{"disambiguationData":[TD([[makeQuery(id+"F0.imprint","IMPRINT",EDGE,{"disambiguationData":[TD([[subQ2,-1.0]])],"derivedFrom":subQ1}),1.0]])]});}
            var Q56;
            {var subQ0=sQuery(id+"F0.wireOp",EDGE,"E9.1.3.0");var subQ1=sQuery(id+"F0.wireOp",EDGE,"E0");var subQ2=makeQuery(id+"F0.imprint","INTERSECT",VERTEX,{"derivedFrom":[subQ1,subQ0]});Q56=makeQuery(id+"F0.imprint","IMPRINT",FACE,{"disambiguationData":[TD([[makeQuery(id+"F0.imprint","IMPRINT",EDGE,{"disambiguationData":[TD([[subQ2,-1.0]])],"derivedFrom":subQ1}),1.0]])]});}
            var Q57;
            {var subQ0=sQuery(id+"F0.wireOp",EDGE,"E8.2.0");var subQ1=sQuery(id+"F0.wireOp",EDGE,"E0");var subQ2=makeQuery(id+"F0.imprint","INTERSECT",VERTEX,{"derivedFrom":[subQ1,subQ0]});Q57=makeQuery(id+"F0.imprint","IMPRINT",FACE,{"disambiguationData":[TD([[makeQuery(id+"F0.imprint","IMPRINT",EDGE,{"disambiguationData":[TD([[subQ2,-1.0]])],"derivedFrom":subQ1}),1.0]])]});}
            var Q58;
            {var subQ0=sQuery(id+"F0.wireOp",EDGE,"E8.1.0");var subQ1=sQuery(id+"F0.wireOp",EDGE,"E0");var subQ2=makeQuery(id+"F0.imprint","INTERSECT",VERTEX,{"derivedFrom":[subQ1,subQ0]});Q58=makeQuery(id+"F0.imprint","IMPRINT",FACE,{"disambiguationData":[TD([[makeQuery(id+"F0.imprint","IMPRINT",EDGE,{"disambiguationData":[TD([[subQ2,-1.0]])],"derivedFrom":subQ1}),1.0]])]});}
            var Q59;
            {var subQ3=sQuery(id+"F0.wireOp",EDGE,"E8.1.1");var subQ5=sQuery(id+"F0.wireOp",EDGE,"E2");var subQ7=makeQuery(id+"F0.imprint","INTERSECT",VERTEX,{"derivedFrom":[subQ5,subQ3]});Q59=makeQuery(id+"F0.imprint","IMPRINT",FACE,{"disambiguationData":[TD([[makeQuery(id+"F0.imprint","IMPRINT",EDGE,{"disambiguationData":[TD([[subQ7,-1.0]])],"derivedFrom":subQ3}),-1.0]])]});}
            var Q60;
            {var subQ0=sQuery(id+"F0.wireOp",EDGE,"E9.1.29.0");var subQ1=sQuery(id+"F0.wireOp",EDGE,"E0");var subQ2=makeQuery(id+"F0.imprint","INTERSECT",VERTEX,{"derivedFrom":[subQ1,subQ0]});Q60=makeQuery(id+"F0.imprint","IMPRINT",FACE,{"disambiguationData":[TD([[makeQuery(id+"F0.imprint","IMPRINT",EDGE,{"disambiguationData":[TD([[subQ2,-1.0]])],"derivedFrom":subQ1}),1.0]])]});}
            extrude(context, id + "F1", {"entities" : qUnion([Q0, Q1, Q2, Q3, Q4, Q5, Q6, Q7, Q8, Q9, Q10, Q11, Q12, Q13, Q14, Q15, Q16, Q17, Q18, Q19, Q20, Q21, Q22, Q23, Q24, Q25, Q26, Q27, Q28, Q29, Q30, Q31, Q32, Q33, Q34, Q35, Q36, Q37, Q38, Q39, Q40, Q41, Q42, Q43, Q44, Q45, Q46, Q47, Q48, Q49, Q50, Q51, Q52, Q53, Q54, Q55, Q56, Q57, Q58, Q59, Q60]), "depth" : 6 * mm, "offsetDistance" : 25 * mm});
        }
        {
            var Q0;
            Q0=makeQuery(id+"F1.opExtrude","CAP_FACE",FACE,{"disambiguationData":[OSD([sQuery(id+"F0.wireOp",EDGE,"E1"),sQuery(id+"F0.wireOp",EDGE,"E2"),sQuery(id+"F0.wireOp",EDGE,"E4"),sQuery(id+"F0.wireOp",EDGE,"E6.trimOffspring"),sQuery(id+"F0.wireOp",EDGE,"E7.MirrorCS"),sQuery(id+"F0.wireOp",EDGE,"E8.1.0"),sQuery(id+"F0.wireOp",EDGE,"E8.1.1"),sQuery(id+"F0.wireOp",EDGE,"E8.2.0"),sQuery(id+"F0.wireOp",EDGE,"E8.2.1"),sQuery(id+"F0.wireOp",EDGE,"E9.1.3.0"),sQuery(id+"F0.wireOp",EDGE,"E9.4.3.0"),sQuery(id+"F0.wireOp",EDGE,"E9.1.4.0"),sQuery(id+"F0.wireOp",EDGE,"E9.4.4.0"),sQuery(id+"F0.wireOp",EDGE,"E9.1.5.0"),sQuery(id+"F0.wireOp",EDGE,"E9.4.5.0"),sQuery(id+"F0.wireOp",EDGE,"E9.1.6.0"),sQuery(id+"F0.wireOp",EDGE,"E9.4.6.0"),sQuery(id+"F0.wireOp",EDGE,"E9.1.7.0"),sQuery(id+"F0.wireOp",EDGE,"E9.4.7.0"),sQuery(id+"F0.wireOp",EDGE,"E9.1.8.0"),sQuery(id+"F0.wireOp",EDGE,"E9.4.8.0"),sQuery(id+"F0.wireOp",EDGE,"E9.1.9.0"),sQuery(id+"F0.wireOp",EDGE,"E9.4.9.0"),sQuery(id+"F0.wireOp",EDGE,"E9.1.10.0"),sQuery(id+"F0.wireOp",EDGE,"E9.4.10.0"),sQuery(id+"F0.wireOp",EDGE,"E9.1.11.0"),sQuery(id+"F0.wireOp",EDGE,"E9.4.11.0"),sQuery(id+"F0.wireOp",EDGE,"E9.1.12.0"),sQuery(id+"F0.wireOp",EDGE,"E9.4.12.0"),sQuery(id+"F0.wireOp",EDGE,"E9.1.13.0"),sQuery(id+"F0.wireOp",EDGE,"E9.4.13.0"),sQuery(id+"F0.wireOp",EDGE,"E9.1.14.0"),sQuery(id+"F0.wireOp",EDGE,"E9.4.14.0"),sQuery(id+"F0.wireOp",EDGE,"E9.1.15.0"),sQuery(id+"F0.wireOp",EDGE,"E9.4.15.0"),sQuery(id+"F0.wireOp",EDGE,"E9.1.16.0"),sQuery(id+"F0.wireOp",EDGE,"E9.4.16.0"),sQuery(id+"F0.wireOp",EDGE,"E9.1.17.0"),sQuery(id+"F0.wireOp",EDGE,"E9.4.17.0"),sQuery(id+"F0.wireOp",EDGE,"E9.1.18.0"),sQuery(id+"F0.wireOp",EDGE,"E9.4.18.0"),sQuery(id+"F0.wireOp",EDGE,"E9.1.19.0"),sQuery(id+"F0.wireOp",EDGE,"E9.4.19.0"),sQuery(id+"F0.wireOp",EDGE,"E9.1.20.0"),sQuery(id+"F0.wireOp",EDGE,"E9.4.20.0"),sQuery(id+"F0.wireOp",EDGE,"E9.1.21.0"),sQuery(id+"F0.wireOp",EDGE,"E9.4.21.0"),sQuery(id+"F0.wireOp",EDGE,"E9.1.22.0"),sQuery(id+"F0.wireOp",EDGE,"E9.4.22.0"),sQuery(id+"F0.wireOp",EDGE,"E9.1.23.0"),sQuery(id+"F0.wireOp",EDGE,"E9.4.23.0"),sQuery(id+"F0.wireOp",EDGE,"E9.1.24.0"),sQuery(id+"F0.wireOp",EDGE,"E9.4.24.0"),sQuery(id+"F0.wireOp",EDGE,"E9.1.25.0"),sQuery(id+"F0.wireOp",EDGE,"E9.4.25.0"),sQuery(id+"F0.wireOp",EDGE,"E9.1.26.0"),sQuery(id+"F0.wireOp",EDGE,"E9.4.26.0"),sQuery(id+"F0.wireOp",EDGE,"E9.1.27.0"),sQuery(id+"F0.wireOp",EDGE,"E9.4.27.0"),sQuery(id+"F0.wireOp",EDGE,"E9.1.28.0"),sQuery(id+"F0.wireOp",EDGE,"E9.4.28.0"),sQuery(id+"F0.wireOp",EDGE,"E9.1.29.0"),sQuery(id+"F0.wireOp",EDGE,"E9.4.29.0")])],"isStart":false});
            var sketch = newSketch(context, id + "F2", { "sketchPlane" : qUnion([Q0])});
            skCircle(sketch, "E10", {"center": v(0, 0) * mm, "radius": 4 * mm});
            skSolve(sketch);
        }
        {
            var Q0;
            Q0 = qSketchRegion(id + "F2", true);
            extrude(context, id + "F3", {"entities" : qUnion([Q0]), "operationType" : NewBodyOperationType.REMOVE, "endBound" : BoundingType.THROUGH_ALL, "oppositeDirection" : true, "depth" : 25 * mm, "offsetDistance" : 25 * mm});
        }
        {
            var Q0;
            Q0=qCreatedBy(makeId("Top.planeOp"),FACE);
            var sketch = newSketch(context, id + "F4", { "sketchPlane" : qUnion([Q0])});
            skLineSegment(sketch, "E11", {"start": v(0, 0) * mm, "end": v(45.2, 0) * mm});
            skCircle(sketch, "E12", {"center": v(45.2, 0) * mm, "radius": 31 * mm});
            skArc(sketch, "E13", {"start": v(45.99, 29.99) * mm, "mid": v(45.2, 30) * mm, "end": v(44.41, 29.99) * mm});
            skArc(sketch, "E14", {"start": v(45.7, 29) * mm, "mid": v(45.2, 29) * mm, "end": v(44.7, 29) * mm});
            skLineSegment(sketch, "E15", {"start": v(45.2, 0) * mm, "end": v(45.2, 46.66) * mm});
            skLineSegment(sketch, "E16", {"start": v(45.2, 30) * mm, "end": v(44.41, 29.99) * mm});
            skLineSegment(sketch, "E17", {"start": v(45.2, 29) * mm, "end": v(44.7, 29) * mm});
            skPoint(sketch, "E18.third.point", {"position": v(13.43, -8.7) * mm});
            skArc(sketch, "E19.trimOffspring", {"start": v(44.7, 29) * mm, "mid": v(44.41, 30) * mm, "end": v(44.1, 30.98) * mm});
            skArc(sketch, "E20.MirrorCS", {"start": v(45.7, 29) * mm, "mid": v(45.99, 30) * mm, "end": v(46.3, 30.98) * mm});
            skArc(sketch, "E21.1.0", {"start": v(42.67, 28.89) * mm, "mid": v(42.85, 29.91) * mm, "end": v(43.06, 30.93) * mm});
            skArc(sketch, "E21.1.1", {"start": v(41.67, 28.78) * mm, "mid": v(41.28, 29.75) * mm, "end": v(40.86, 30.7) * mm});
            skArc(sketch, "E21.2.0", {"start": v(39.66, 28.47) * mm, "mid": v(39.73, 29.5) * mm, "end": v(39.84, 30.53) * mm});
            skArc(sketch, "E21.2.1", {"start": v(38.68, 28.26) * mm, "mid": v(38.2, 29.17) * mm, "end": v(37.68, 30.07) * mm});
            skArc(sketch, "E21.3.0", {"start": v(36.72, 27.73) * mm, "mid": v(36.68, 28.77) * mm, "end": v(36.68, 29.8) * mm});
            skArc(sketch, "E21.3.1", {"start": v(35.76, 27.42) * mm, "mid": v(35.18, 28.28) * mm, "end": v(34.57, 29.12) * mm});
            skArc(sketch, "E21.4.0", {"start": v(33.86, 26.7) * mm, "mid": v(33.72, 27.72) * mm, "end": v(33.61, 28.75) * mm});
            skArc(sketch, "E21.4.1", {"start": v(32.95, 26.29) * mm, "mid": v(32.28, 27.08) * mm, "end": v(31.59, 27.85) * mm});
            skArc(sketch, "E21.5.0", {"start": v(31.14, 25.36) * mm, "mid": v(30.88, 26.37) * mm, "end": v(30.67, 27.38) * mm});
            skArc(sketch, "E21.5.1", {"start": v(30.27, 24.86) * mm, "mid": v(29.52, 25.58) * mm, "end": v(28.75, 26.28) * mm});
            skArc(sketch, "E21.6.0", {"start": v(28.56, 23.75) * mm, "mid": v(28.2, 24.73) * mm, "end": v(27.89, 25.71) * mm});
            skArc(sketch, "E21.6.1", {"start": v(27.75, 23.16) * mm, "mid": v(26.93, 23.8) * mm, "end": v(26.1, 24.41) * mm});
            skArc(sketch, "E21.7.0", {"start": v(26.17, 21.88) * mm, "mid": v(25.72, 22.82) * mm, "end": v(25.3, 23.76) * mm});
            skArc(sketch, "E21.7.1", {"start": v(25.43, 21.21) * mm, "mid": v(24.55, 21.76) * mm, "end": v(23.65, 22.28) * mm});
            skArc(sketch, "E21.8.0", {"start": v(23.99, 19.77) * mm, "mid": v(23.44, 20.65) * mm, "end": v(22.92, 21.55) * mm});
            skArc(sketch, "E21.8.1", {"start": v(23.32, 19.03) * mm, "mid": v(22.38, 19.48) * mm, "end": v(21.44, 19.9) * mm});
            skArc(sketch, "E21.9.0", {"start": v(22.04, 17.45) * mm, "mid": v(21.4, 18.27) * mm, "end": v(20.79, 19.1) * mm});
            skArc(sketch, "E21.9.1", {"start": v(21.45, 16.64) * mm, "mid": v(20.47, 17) * mm, "end": v(19.49, 17.31) * mm});
            skArc(sketch, "E21.10.0", {"start": v(20.34, 14.93) * mm, "mid": v(19.62, 15.68) * mm, "end": v(18.92, 16.45) * mm});
            skArc(sketch, "E21.10.1", {"start": v(19.84, 14.06) * mm, "mid": v(18.83, 14.32) * mm, "end": v(17.82, 14.53) * mm});
            skArc(sketch, "E21.11.0", {"start": v(18.91, 12.25) * mm, "mid": v(18.12, 12.92) * mm, "end": v(17.35, 13.61) * mm});
            skArc(sketch, "E21.11.1", {"start": v(18.5, 11.34) * mm, "mid": v(17.48, 11.48) * mm, "end": v(16.45, 11.59) * mm});
            skArc(sketch, "E21.12.0", {"start": v(17.78, 9.44) * mm, "mid": v(16.92, 10.02) * mm, "end": v(16.08, 10.63) * mm});
            skArc(sketch, "E21.12.1", {"start": v(17.47, 8.48) * mm, "mid": v(16.43, 8.52) * mm, "end": v(15.4, 8.52) * mm});
            skArc(sketch, "E21.13.0", {"start": v(16.94, 6.52) * mm, "mid": v(16.03, 7) * mm, "end": v(15.13, 7.52) * mm});
            skArc(sketch, "E21.13.1", {"start": v(16.73, 5.54) * mm, "mid": v(15.7, 5.47) * mm, "end": v(14.67, 5.36) * mm});
            skArc(sketch, "E21.14.0", {"start": v(16.42, 3.53) * mm, "mid": v(15.45, 3.92) * mm, "end": v(14.5, 4.34) * mm});
            skArc(sketch, "E21.14.1", {"start": v(16.31, 2.53) * mm, "mid": v(15.29, 2.35) * mm, "end": v(14.27, 2.14) * mm});
            skArc(sketch, "E21.15.0", {"start": v(16.2, 0.5) * mm, "mid": v(15.2, 0.79) * mm, "end": v(14.22, 1.1) * mm});
            skArc(sketch, "E21.15.1", {"start": v(16.2, -0.5) * mm, "mid": v(15.2, -0.79) * mm, "end": v(14.22, -1.1) * mm});
            skArc(sketch, "E21.16.0", {"start": v(16.31, -2.53) * mm, "mid": v(15.29, -2.35) * mm, "end": v(14.27, -2.14) * mm});
            skArc(sketch, "E21.16.1", {"start": v(16.42, -3.53) * mm, "mid": v(15.45, -3.92) * mm, "end": v(14.5, -4.34) * mm});
            skArc(sketch, "E21.17.0", {"start": v(16.73, -5.54) * mm, "mid": v(15.7, -5.47) * mm, "end": v(14.67, -5.36) * mm});
            skArc(sketch, "E21.17.1", {"start": v(16.94, -6.52) * mm, "mid": v(16.03, -7) * mm, "end": v(15.13, -7.52) * mm});
            skArc(sketch, "E21.18.0", {"start": v(17.47, -8.48) * mm, "mid": v(16.43, -8.52) * mm, "end": v(15.4, -8.52) * mm});
            skArc(sketch, "E21.18.1", {"start": v(17.78, -9.44) * mm, "mid": v(16.92, -10.02) * mm, "end": v(16.08, -10.63) * mm});
            skArc(sketch, "E21.19.0", {"start": v(18.5, -11.34) * mm, "mid": v(17.48, -11.48) * mm, "end": v(16.45, -11.59) * mm});
            skArc(sketch, "E21.19.1", {"start": v(18.91, -12.25) * mm, "mid": v(18.12, -12.92) * mm, "end": v(17.35, -13.61) * mm});
            skArc(sketch, "E21.20.0", {"start": v(19.84, -14.06) * mm, "mid": v(18.83, -14.32) * mm, "end": v(17.82, -14.53) * mm});
            skArc(sketch, "E21.20.1", {"start": v(20.34, -14.93) * mm, "mid": v(19.62, -15.68) * mm, "end": v(18.92, -16.45) * mm});
            skArc(sketch, "E21.21.0", {"start": v(21.45, -16.64) * mm, "mid": v(20.47, -17) * mm, "end": v(19.49, -17.31) * mm});
            skArc(sketch, "E21.21.1", {"start": v(22.04, -17.45) * mm, "mid": v(21.4, -18.27) * mm, "end": v(20.79, -19.1) * mm});
            skArc(sketch, "E21.22.0", {"start": v(23.32, -19.03) * mm, "mid": v(22.38, -19.48) * mm, "end": v(21.44, -19.9) * mm});
            skArc(sketch, "E21.22.1", {"start": v(23.99, -19.77) * mm, "mid": v(23.44, -20.65) * mm, "end": v(22.92, -21.55) * mm});
            skArc(sketch, "E21.23.0", {"start": v(25.43, -21.21) * mm, "mid": v(24.55, -21.76) * mm, "end": v(23.65, -22.28) * mm});
            skArc(sketch, "E21.23.1", {"start": v(26.17, -21.88) * mm, "mid": v(25.72, -22.82) * mm, "end": v(25.3, -23.76) * mm});
            skArc(sketch, "E21.24.0", {"start": v(27.75, -23.16) * mm, "mid": v(26.93, -23.8) * mm, "end": v(26.1, -24.41) * mm});
            skArc(sketch, "E21.24.1", {"start": v(28.56, -23.75) * mm, "mid": v(28.2, -24.73) * mm, "end": v(27.89, -25.71) * mm});
            skArc(sketch, "E21.25.0", {"start": v(30.27, -24.86) * mm, "mid": v(29.52, -25.58) * mm, "end": v(28.75, -26.28) * mm});
            skArc(sketch, "E21.25.1", {"start": v(31.14, -25.36) * mm, "mid": v(30.88, -26.37) * mm, "end": v(30.67, -27.38) * mm});
            skArc(sketch, "E21.26.0", {"start": v(32.95, -26.29) * mm, "mid": v(32.28, -27.08) * mm, "end": v(31.59, -27.85) * mm});
            skArc(sketch, "E21.26.1", {"start": v(33.86, -26.7) * mm, "mid": v(33.72, -27.72) * mm, "end": v(33.61, -28.75) * mm});
            skArc(sketch, "E21.27.0", {"start": v(35.76, -27.42) * mm, "mid": v(35.18, -28.28) * mm, "end": v(34.57, -29.12) * mm});
            skArc(sketch, "E21.27.1", {"start": v(36.72, -27.73) * mm, "mid": v(36.68, -28.77) * mm, "end": v(36.68, -29.8) * mm});
            skArc(sketch, "E21.28.0", {"start": v(38.68, -28.26) * mm, "mid": v(38.2, -29.17) * mm, "end": v(37.68, -30.07) * mm});
            skArc(sketch, "E21.28.1", {"start": v(39.66, -28.47) * mm, "mid": v(39.73, -29.5) * mm, "end": v(39.84, -30.53) * mm});
            skArc(sketch, "E21.29.0", {"start": v(41.67, -28.78) * mm, "mid": v(41.28, -29.75) * mm, "end": v(40.86, -30.7) * mm});
            skArc(sketch, "E21.29.1", {"start": v(42.67, -28.89) * mm, "mid": v(42.85, -29.91) * mm, "end": v(43.06, -30.93) * mm});
            skArc(sketch, "E21.30.0", {"start": v(44.7, -29) * mm, "mid": v(44.41, -30) * mm, "end": v(44.1, -30.98) * mm});
            skArc(sketch, "E21.30.1", {"start": v(45.7, -29) * mm, "mid": v(45.99, -30) * mm, "end": v(46.3, -30.98) * mm});
            skArc(sketch, "E21.31.0", {"start": v(47.73, -28.89) * mm, "mid": v(47.55, -29.91) * mm, "end": v(47.34, -30.93) * mm});
            skArc(sketch, "E21.31.1", {"start": v(48.73, -28.78) * mm, "mid": v(49.12, -29.75) * mm, "end": v(49.54, -30.7) * mm});
            skArc(sketch, "E21.32.0", {"start": v(50.74, -28.47) * mm, "mid": v(50.67, -29.5) * mm, "end": v(50.56, -30.53) * mm});
            skArc(sketch, "E21.32.1", {"start": v(51.72, -28.26) * mm, "mid": v(52.2, -29.17) * mm, "end": v(52.72, -30.07) * mm});
            skArc(sketch, "E21.33.0", {"start": v(53.68, -27.73) * mm, "mid": v(53.72, -28.77) * mm, "end": v(53.72, -29.8) * mm});
            skArc(sketch, "E21.33.1", {"start": v(54.64, -27.42) * mm, "mid": v(55.22, -28.28) * mm, "end": v(55.83, -29.12) * mm});
            skArc(sketch, "E21.34.0", {"start": v(56.54, -26.7) * mm, "mid": v(56.68, -27.72) * mm, "end": v(56.79, -28.75) * mm});
            skArc(sketch, "E21.34.1", {"start": v(57.45, -26.29) * mm, "mid": v(58.12, -27.08) * mm, "end": v(58.81, -27.85) * mm});
            skArc(sketch, "E21.35.0", {"start": v(59.26, -25.36) * mm, "mid": v(59.52, -26.37) * mm, "end": v(59.73, -27.38) * mm});
            skArc(sketch, "E21.35.1", {"start": v(60.13, -24.86) * mm, "mid": v(60.88, -25.58) * mm, "end": v(61.65, -26.28) * mm});
            skArc(sketch, "E21.36.0", {"start": v(61.84, -23.75) * mm, "mid": v(62.2, -24.73) * mm, "end": v(62.51, -25.71) * mm});
            skArc(sketch, "E21.36.1", {"start": v(62.65, -23.16) * mm, "mid": v(63.47, -23.8) * mm, "end": v(64.3, -24.41) * mm});
            skArc(sketch, "E21.37.0", {"start": v(64.23, -21.88) * mm, "mid": v(64.68, -22.82) * mm, "end": v(65.1, -23.76) * mm});
            skArc(sketch, "E21.37.1", {"start": v(64.97, -21.21) * mm, "mid": v(65.85, -21.76) * mm, "end": v(66.75, -22.28) * mm});
            skArc(sketch, "E21.38.0", {"start": v(66.41, -19.77) * mm, "mid": v(66.96, -20.65) * mm, "end": v(67.48, -21.55) * mm});
            skArc(sketch, "E21.38.1", {"start": v(67.08, -19.03) * mm, "mid": v(68.02, -19.48) * mm, "end": v(68.96, -19.9) * mm});
            skArc(sketch, "E21.39.0", {"start": v(68.36, -17.45) * mm, "mid": v(69, -18.27) * mm, "end": v(69.61, -19.1) * mm});
            skArc(sketch, "E21.39.1", {"start": v(68.95, -16.64) * mm, "mid": v(69.93, -17) * mm, "end": v(70.91, -17.31) * mm});
            skArc(sketch, "E21.40.0", {"start": v(70.06, -14.93) * mm, "mid": v(70.78, -15.68) * mm, "end": v(71.48, -16.45) * mm});
            skArc(sketch, "E21.40.1", {"start": v(70.56, -14.06) * mm, "mid": v(71.57, -14.32) * mm, "end": v(72.58, -14.53) * mm});
            skArc(sketch, "E21.41.0", {"start": v(71.49, -12.25) * mm, "mid": v(72.28, -12.92) * mm, "end": v(73.05, -13.61) * mm});
            skArc(sketch, "E21.41.1", {"start": v(71.9, -11.34) * mm, "mid": v(72.92, -11.48) * mm, "end": v(73.95, -11.59) * mm});
            skArc(sketch, "E21.42.0", {"start": v(72.62, -9.44) * mm, "mid": v(73.48, -10.02) * mm, "end": v(74.32, -10.63) * mm});
            skArc(sketch, "E21.42.1", {"start": v(72.93, -8.48) * mm, "mid": v(73.97, -8.52) * mm, "end": v(75, -8.52) * mm});
            skArc(sketch, "E21.43.0", {"start": v(73.46, -6.52) * mm, "mid": v(74.37, -7) * mm, "end": v(75.27, -7.52) * mm});
            skArc(sketch, "E21.43.1", {"start": v(73.67, -5.54) * mm, "mid": v(74.7, -5.47) * mm, "end": v(75.73, -5.36) * mm});
            skArc(sketch, "E21.44.0", {"start": v(73.98, -3.53) * mm, "mid": v(74.95, -3.92) * mm, "end": v(75.9, -4.34) * mm});
            skArc(sketch, "E21.44.1", {"start": v(74.09, -2.53) * mm, "mid": v(75.11, -2.35) * mm, "end": v(76.13, -2.14) * mm});
            skArc(sketch, "E21.45.0", {"start": v(74.2, -0.5) * mm, "mid": v(75.2, -0.79) * mm, "end": v(76.18, -1.1) * mm});
            skArc(sketch, "E21.45.1", {"start": v(74.2, 0.5) * mm, "mid": v(75.2, 0.79) * mm, "end": v(76.18, 1.1) * mm});
            skArc(sketch, "E21.46.0", {"start": v(74.09, 2.53) * mm, "mid": v(75.11, 2.35) * mm, "end": v(76.13, 2.14) * mm});
            skArc(sketch, "E21.46.1", {"start": v(73.98, 3.53) * mm, "mid": v(74.95, 3.92) * mm, "end": v(75.9, 4.34) * mm});
            skArc(sketch, "E21.47.0", {"start": v(73.67, 5.54) * mm, "mid": v(74.7, 5.47) * mm, "end": v(75.73, 5.36) * mm});
            skArc(sketch, "E21.47.1", {"start": v(73.46, 6.52) * mm, "mid": v(74.37, 7) * mm, "end": v(75.27, 7.52) * mm});
            skArc(sketch, "E21.48.0", {"start": v(72.93, 8.48) * mm, "mid": v(73.97, 8.52) * mm, "end": v(75, 8.52) * mm});
            skArc(sketch, "E21.48.1", {"start": v(72.62, 9.44) * mm, "mid": v(73.48, 10.02) * mm, "end": v(74.32, 10.63) * mm});
            skArc(sketch, "E21.49.0", {"start": v(71.9, 11.34) * mm, "mid": v(72.92, 11.48) * mm, "end": v(73.95, 11.59) * mm});
            skArc(sketch, "E21.49.1", {"start": v(71.49, 12.25) * mm, "mid": v(72.28, 12.92) * mm, "end": v(73.05, 13.61) * mm});
            skArc(sketch, "E21.50.0", {"start": v(70.56, 14.06) * mm, "mid": v(71.57, 14.32) * mm, "end": v(72.58, 14.53) * mm});
            skArc(sketch, "E21.50.1", {"start": v(70.06, 14.93) * mm, "mid": v(70.78, 15.68) * mm, "end": v(71.48, 16.45) * mm});
            skArc(sketch, "E21.51.0", {"start": v(68.95, 16.64) * mm, "mid": v(69.93, 17) * mm, "end": v(70.91, 17.31) * mm});
            skArc(sketch, "E21.51.1", {"start": v(68.36, 17.45) * mm, "mid": v(69, 18.27) * mm, "end": v(69.61, 19.1) * mm});
            skArc(sketch, "E21.52.0", {"start": v(67.08, 19.03) * mm, "mid": v(68.02, 19.48) * mm, "end": v(68.96, 19.9) * mm});
            skArc(sketch, "E21.52.1", {"start": v(66.41, 19.77) * mm, "mid": v(66.96, 20.65) * mm, "end": v(67.48, 21.55) * mm});
            skArc(sketch, "E21.53.0", {"start": v(64.97, 21.21) * mm, "mid": v(65.85, 21.76) * mm, "end": v(66.75, 22.28) * mm});
            skArc(sketch, "E21.53.1", {"start": v(64.23, 21.88) * mm, "mid": v(64.68, 22.82) * mm, "end": v(65.1, 23.76) * mm});
            skArc(sketch, "E21.54.0", {"start": v(62.65, 23.16) * mm, "mid": v(63.47, 23.8) * mm, "end": v(64.3, 24.41) * mm});
            skArc(sketch, "E21.54.1", {"start": v(61.84, 23.75) * mm, "mid": v(62.2, 24.73) * mm, "end": v(62.51, 25.71) * mm});
            skArc(sketch, "E21.55.0", {"start": v(60.13, 24.86) * mm, "mid": v(60.88, 25.58) * mm, "end": v(61.65, 26.28) * mm});
            skArc(sketch, "E21.55.1", {"start": v(59.26, 25.36) * mm, "mid": v(59.52, 26.37) * mm, "end": v(59.73, 27.38) * mm});
            skArc(sketch, "E21.56.0", {"start": v(57.45, 26.29) * mm, "mid": v(58.12, 27.08) * mm, "end": v(58.81, 27.85) * mm});
            skArc(sketch, "E21.56.1", {"start": v(56.54, 26.7) * mm, "mid": v(56.68, 27.72) * mm, "end": v(56.79, 28.75) * mm});
            skArc(sketch, "E21.57.0", {"start": v(54.64, 27.42) * mm, "mid": v(55.22, 28.28) * mm, "end": v(55.83, 29.12) * mm});
            skArc(sketch, "E21.57.1", {"start": v(53.68, 27.73) * mm, "mid": v(53.72, 28.77) * mm, "end": v(53.72, 29.8) * mm});
            skArc(sketch, "E21.58.0", {"start": v(51.72, 28.26) * mm, "mid": v(52.2, 29.17) * mm, "end": v(52.72, 30.07) * mm});
            skArc(sketch, "E21.58.1", {"start": v(50.74, 28.47) * mm, "mid": v(50.67, 29.5) * mm, "end": v(50.56, 30.53) * mm});
            skArc(sketch, "E21.59.0", {"start": v(48.73, 28.78) * mm, "mid": v(49.12, 29.75) * mm, "end": v(49.54, 30.7) * mm});
            skArc(sketch, "E21.59.1", {"start": v(47.73, 28.89) * mm, "mid": v(47.55, 29.91) * mm, "end": v(47.34, 30.93) * mm});
            skCircle(sketch, "E22", {"center": v(45.2, 0) * mm, "radius": 29 * mm});
            skSolve(sketch);
        }
        {
            var Q0;
            {var subQ0=sQuery(id+"F4.wireOp",EDGE,"E21.30.1");Q0=makeQuery(id+"F4.imprint","IMPRINT",FACE,{"disambiguationData":[TD([[makeQuery(id+"F4.imprint","IMPRINT",EDGE,{"derivedFrom":subQ0}),1.0]])]});}
            var Q1;
            {var subQ0=sQuery(id+"F4.wireOp",EDGE,"E21.26.1");Q1=makeQuery(id+"F4.imprint","IMPRINT",FACE,{"disambiguationData":[TD([[makeQuery(id+"F4.imprint","IMPRINT",EDGE,{"derivedFrom":subQ0}),1.0]])]});}
            var Q2;
            {var subQ13=sQuery(id+"F4.wireOp",EDGE,"E17");Q2=makeQuery(id+"F4.imprint","IMPRINT",FACE,{"disambiguationData":[TD([[makeQuery(id+"F4.imprint","IMPRINT",EDGE,{"derivedFrom":subQ13}),1.0]])]});}
            var Q3;
            {var subQ0=sQuery(id+"F4.wireOp",EDGE,"E21.40.1");Q3=makeQuery(id+"F4.imprint","IMPRINT",FACE,{"disambiguationData":[TD([[makeQuery(id+"F4.imprint","IMPRINT",EDGE,{"derivedFrom":subQ0}),1.0]])]});}
            var Q4;
            {var subQ0=sQuery(id+"F4.wireOp",EDGE,"E21.10.1");Q4=makeQuery(id+"F4.imprint","IMPRINT",FACE,{"disambiguationData":[TD([[makeQuery(id+"F4.imprint","IMPRINT",EDGE,{"derivedFrom":subQ0}),1.0]])]});}
            var Q5;
            {var subQ0=sQuery(id+"F4.wireOp",EDGE,"E21.54.1");Q5=makeQuery(id+"F4.imprint","IMPRINT",FACE,{"disambiguationData":[TD([[makeQuery(id+"F4.imprint","IMPRINT",EDGE,{"derivedFrom":subQ0}),1.0]])]});}
            var Q6;
            {var subQ0=sQuery(id+"F4.wireOp",EDGE,"E21.14.1");Q6=makeQuery(id+"F4.imprint","IMPRINT",FACE,{"disambiguationData":[TD([[makeQuery(id+"F4.imprint","IMPRINT",EDGE,{"derivedFrom":subQ0}),1.0]])]});}
            var Q7;
            {var subQ0=sQuery(id+"F4.wireOp",EDGE,"E21.2.1");Q7=makeQuery(id+"F4.imprint","IMPRINT",FACE,{"disambiguationData":[TD([[makeQuery(id+"F4.imprint","IMPRINT",EDGE,{"derivedFrom":subQ0}),1.0]])]});}
            var Q8;
            {var subQ0=sQuery(id+"F4.wireOp",EDGE,"E21.44.1");Q8=makeQuery(id+"F4.imprint","IMPRINT",FACE,{"disambiguationData":[TD([[makeQuery(id+"F4.imprint","IMPRINT",EDGE,{"derivedFrom":subQ0}),1.0]])]});}
            var Q9;
            {var subQ0=sQuery(id+"F4.wireOp",EDGE,"E21.31.1");Q9=makeQuery(id+"F4.imprint","IMPRINT",FACE,{"disambiguationData":[TD([[makeQuery(id+"F4.imprint","IMPRINT",EDGE,{"derivedFrom":subQ0}),1.0]])]});}
            var Q10;
            {var subQ0=sQuery(id+"F4.wireOp",EDGE,"E21.58.1");Q10=makeQuery(id+"F4.imprint","IMPRINT",FACE,{"disambiguationData":[TD([[makeQuery(id+"F4.imprint","IMPRINT",EDGE,{"derivedFrom":subQ0}),1.0]])]});}
            var Q11;
            {var subQ0=sQuery(id+"F4.wireOp",EDGE,"E21.17.1");Q11=makeQuery(id+"F4.imprint","IMPRINT",FACE,{"disambiguationData":[TD([[makeQuery(id+"F4.imprint","IMPRINT",EDGE,{"derivedFrom":subQ0}),1.0]])]});}
            var Q12;
            {var subQ0=sQuery(id+"F4.wireOp",EDGE,"E21.22.1");Q12=makeQuery(id+"F4.imprint","IMPRINT",FACE,{"disambiguationData":[TD([[makeQuery(id+"F4.imprint","IMPRINT",EDGE,{"derivedFrom":subQ0}),1.0]])]});}
            var Q13;
            {var subQ0=sQuery(id+"F4.wireOp",EDGE,"E21.41.1");Q13=makeQuery(id+"F4.imprint","IMPRINT",FACE,{"disambiguationData":[TD([[makeQuery(id+"F4.imprint","IMPRINT",EDGE,{"derivedFrom":subQ0}),1.0]])]});}
            var Q14;
            {var subQ0=sQuery(id+"F4.wireOp",EDGE,"E21.45.1");Q14=makeQuery(id+"F4.imprint","IMPRINT",FACE,{"disambiguationData":[TD([[makeQuery(id+"F4.imprint","IMPRINT",EDGE,{"derivedFrom":subQ0}),1.0]])]});}
            var Q15;
            {var subQ0=sQuery(id+"F4.wireOp",EDGE,"E21.18.1");Q15=makeQuery(id+"F4.imprint","IMPRINT",FACE,{"disambiguationData":[TD([[makeQuery(id+"F4.imprint","IMPRINT",EDGE,{"derivedFrom":subQ0}),1.0]])]});}
            var Q16;
            {var subQ0=sQuery(id+"F4.wireOp",EDGE,"E21.19.1");Q16=makeQuery(id+"F4.imprint","IMPRINT",FACE,{"disambiguationData":[TD([[makeQuery(id+"F4.imprint","IMPRINT",EDGE,{"derivedFrom":subQ0}),1.0]])]});}
            var Q17;
            {var subQ0=sQuery(id+"F4.wireOp",EDGE,"E21.57.1");Q17=makeQuery(id+"F4.imprint","IMPRINT",FACE,{"disambiguationData":[TD([[makeQuery(id+"F4.imprint","IMPRINT",EDGE,{"derivedFrom":subQ0}),1.0]])]});}
            var Q18;
            {var subQ0=sQuery(id+"F4.wireOp",EDGE,"E21.9.1");Q18=makeQuery(id+"F4.imprint","IMPRINT",FACE,{"disambiguationData":[TD([[makeQuery(id+"F4.imprint","IMPRINT",EDGE,{"derivedFrom":subQ0}),1.0]])]});}
            var Q19;
            {var subQ0=sQuery(id+"F4.wireOp",EDGE,"E21.59.1");Q19=makeQuery(id+"F4.imprint","IMPRINT",FACE,{"disambiguationData":[TD([[makeQuery(id+"F4.imprint","IMPRINT",EDGE,{"derivedFrom":subQ0}),1.0]])]});}
            var Q20;
            {var subQ0=sQuery(id+"F4.wireOp",EDGE,"E21.11.1");Q20=makeQuery(id+"F4.imprint","IMPRINT",FACE,{"disambiguationData":[TD([[makeQuery(id+"F4.imprint","IMPRINT",EDGE,{"derivedFrom":subQ0}),1.0]])]});}
            var Q21;
            {var subQ0=sQuery(id+"F4.wireOp",EDGE,"E21.52.1");Q21=makeQuery(id+"F4.imprint","IMPRINT",FACE,{"disambiguationData":[TD([[makeQuery(id+"F4.imprint","IMPRINT",EDGE,{"derivedFrom":subQ0}),1.0]])]});}
            var Q22;
            {var subQ0=sQuery(id+"F4.wireOp",EDGE,"E21.38.1");Q22=makeQuery(id+"F4.imprint","IMPRINT",FACE,{"disambiguationData":[TD([[makeQuery(id+"F4.imprint","IMPRINT",EDGE,{"derivedFrom":subQ0}),1.0]])]});}
            var Q23;
            {var subQ0=sQuery(id+"F4.wireOp",EDGE,"E21.34.1");Q23=makeQuery(id+"F4.imprint","IMPRINT",FACE,{"disambiguationData":[TD([[makeQuery(id+"F4.imprint","IMPRINT",EDGE,{"derivedFrom":subQ0}),1.0]])]});}
            var Q24;
            {var subQ0=sQuery(id+"F4.wireOp",EDGE,"E21.49.1");Q24=makeQuery(id+"F4.imprint","IMPRINT",FACE,{"disambiguationData":[TD([[makeQuery(id+"F4.imprint","IMPRINT",EDGE,{"derivedFrom":subQ0}),1.0]])]});}
            var Q25;
            {var subQ0=sQuery(id+"F4.wireOp",EDGE,"E21.1.0");Q25=makeQuery(id+"F4.imprint","IMPRINT",FACE,{"disambiguationData":[TD([[makeQuery(id+"F4.imprint","IMPRINT",EDGE,{"derivedFrom":subQ0}),-1.0]])]});}
            var Q26;
            {var subQ1=sQuery(id+"F4.wireOp",EDGE,"E15");var subQ26=sQuery(id+"F4.wireOp",EDGE,"E11");var subQ27=makeQuery(id+"F4.imprint","INTERSECT",VERTEX,{"derivedFrom":[subQ26,subQ1]});Q26=makeQuery(id+"F4.imprint","IMPRINT",FACE,{"disambiguationData":[TD([[makeQuery(id+"F4.imprint","IMPRINT",EDGE,{"disambiguationData":[TD([[subQ27,1.0]])],"derivedFrom":subQ26}),-1.0]])]});}
            var Q27;
            {var subQ0=sQuery(id+"F4.wireOp",EDGE,"E21.46.1");Q27=makeQuery(id+"F4.imprint","IMPRINT",FACE,{"disambiguationData":[TD([[makeQuery(id+"F4.imprint","IMPRINT",EDGE,{"derivedFrom":subQ0}),1.0]])]});}
            var Q28;
            {var subQ0=sQuery(id+"F4.wireOp",EDGE,"E21.32.1");Q28=makeQuery(id+"F4.imprint","IMPRINT",FACE,{"disambiguationData":[TD([[makeQuery(id+"F4.imprint","IMPRINT",EDGE,{"derivedFrom":subQ0}),1.0]])]});}
            var Q29;
            {var subQ0=sQuery(id+"F4.wireOp",EDGE,"E21.7.1");Q29=makeQuery(id+"F4.imprint","IMPRINT",FACE,{"disambiguationData":[TD([[makeQuery(id+"F4.imprint","IMPRINT",EDGE,{"derivedFrom":subQ0}),1.0]])]});}
            var Q30;
            {var subQ0=sQuery(id+"F4.wireOp",EDGE,"E21.15.1");Q30=makeQuery(id+"F4.imprint","IMPRINT",FACE,{"disambiguationData":[TD([[makeQuery(id+"F4.imprint","IMPRINT",EDGE,{"derivedFrom":subQ0}),1.0]])]});}
            var Q31;
            {var subQ0=sQuery(id+"F4.wireOp",EDGE,"E21.25.1");Q31=makeQuery(id+"F4.imprint","IMPRINT",FACE,{"disambiguationData":[TD([[makeQuery(id+"F4.imprint","IMPRINT",EDGE,{"derivedFrom":subQ0}),1.0]])]});}
            var Q32;
            {var subQ0=sQuery(id+"F4.wireOp",EDGE,"E21.4.1");Q32=makeQuery(id+"F4.imprint","IMPRINT",FACE,{"disambiguationData":[TD([[makeQuery(id+"F4.imprint","IMPRINT",EDGE,{"derivedFrom":subQ0}),1.0]])]});}
            var Q33;
            {var subQ0=sQuery(id+"F4.wireOp",EDGE,"E21.37.1");Q33=makeQuery(id+"F4.imprint","IMPRINT",FACE,{"disambiguationData":[TD([[makeQuery(id+"F4.imprint","IMPRINT",EDGE,{"derivedFrom":subQ0}),1.0]])]});}
            var Q34;
            {var subQ0=sQuery(id+"F4.wireOp",EDGE,"E21.43.1");Q34=makeQuery(id+"F4.imprint","IMPRINT",FACE,{"disambiguationData":[TD([[makeQuery(id+"F4.imprint","IMPRINT",EDGE,{"derivedFrom":subQ0}),1.0]])]});}
            var Q35;
            {var subQ0=sQuery(id+"F4.wireOp",EDGE,"E21.47.1");Q35=makeQuery(id+"F4.imprint","IMPRINT",FACE,{"disambiguationData":[TD([[makeQuery(id+"F4.imprint","IMPRINT",EDGE,{"derivedFrom":subQ0}),1.0]])]});}
            var Q36;
            {var subQ0=sQuery(id+"F4.wireOp",EDGE,"E21.55.1");Q36=makeQuery(id+"F4.imprint","IMPRINT",FACE,{"disambiguationData":[TD([[makeQuery(id+"F4.imprint","IMPRINT",EDGE,{"derivedFrom":subQ0}),1.0]])]});}
            var Q37;
            {var subQ0=sQuery(id+"F4.wireOp",EDGE,"E21.53.1");Q37=makeQuery(id+"F4.imprint","IMPRINT",FACE,{"disambiguationData":[TD([[makeQuery(id+"F4.imprint","IMPRINT",EDGE,{"derivedFrom":subQ0}),1.0]])]});}
            var Q38;
            {var subQ0=sQuery(id+"F4.wireOp",EDGE,"E21.5.1");Q38=makeQuery(id+"F4.imprint","IMPRINT",FACE,{"disambiguationData":[TD([[makeQuery(id+"F4.imprint","IMPRINT",EDGE,{"derivedFrom":subQ0}),1.0]])]});}
            var Q39;
            {var subQ0=sQuery(id+"F4.wireOp",EDGE,"E21.35.1");Q39=makeQuery(id+"F4.imprint","IMPRINT",FACE,{"disambiguationData":[TD([[makeQuery(id+"F4.imprint","IMPRINT",EDGE,{"derivedFrom":subQ0}),1.0]])]});}
            var Q40;
            {var subQ0=sQuery(id+"F4.wireOp",EDGE,"E21.51.1");Q40=makeQuery(id+"F4.imprint","IMPRINT",FACE,{"disambiguationData":[TD([[makeQuery(id+"F4.imprint","IMPRINT",EDGE,{"derivedFrom":subQ0}),1.0]])]});}
            var Q41;
            {var subQ0=sQuery(id+"F4.wireOp",EDGE,"E21.16.1");Q41=makeQuery(id+"F4.imprint","IMPRINT",FACE,{"disambiguationData":[TD([[makeQuery(id+"F4.imprint","IMPRINT",EDGE,{"derivedFrom":subQ0}),1.0]])]});}
            var Q42;
            {var subQ0=sQuery(id+"F4.wireOp",EDGE,"E21.1.1");Q42=makeQuery(id+"F4.imprint","IMPRINT",FACE,{"disambiguationData":[TD([[makeQuery(id+"F4.imprint","IMPRINT",EDGE,{"derivedFrom":subQ0}),1.0]])]});}
            var Q43;
            {var subQ0=sQuery(id+"F4.wireOp",EDGE,"E21.27.1");Q43=makeQuery(id+"F4.imprint","IMPRINT",FACE,{"disambiguationData":[TD([[makeQuery(id+"F4.imprint","IMPRINT",EDGE,{"derivedFrom":subQ0}),1.0]])]});}
            var Q44;
            {var subQ0=sQuery(id+"F4.wireOp",EDGE,"E21.6.1");Q44=makeQuery(id+"F4.imprint","IMPRINT",FACE,{"disambiguationData":[TD([[makeQuery(id+"F4.imprint","IMPRINT",EDGE,{"derivedFrom":subQ0}),1.0]])]});}
            var Q45;
            {var subQ0=sQuery(id+"F4.wireOp",EDGE,"E21.50.1");Q45=makeQuery(id+"F4.imprint","IMPRINT",FACE,{"disambiguationData":[TD([[makeQuery(id+"F4.imprint","IMPRINT",EDGE,{"derivedFrom":subQ0}),1.0]])]});}
            var Q46;
            {var subQ0=sQuery(id+"F4.wireOp",EDGE,"E21.29.1");Q46=makeQuery(id+"F4.imprint","IMPRINT",FACE,{"disambiguationData":[TD([[makeQuery(id+"F4.imprint","IMPRINT",EDGE,{"derivedFrom":subQ0}),1.0]])]});}
            var Q47;
            {var subQ0=sQuery(id+"F4.wireOp",EDGE,"E21.8.1");Q47=makeQuery(id+"F4.imprint","IMPRINT",FACE,{"disambiguationData":[TD([[makeQuery(id+"F4.imprint","IMPRINT",EDGE,{"derivedFrom":subQ0}),1.0]])]});}
            var Q48;
            {var subQ0=sQuery(id+"F4.wireOp",EDGE,"E21.28.1");Q48=makeQuery(id+"F4.imprint","IMPRINT",FACE,{"disambiguationData":[TD([[makeQuery(id+"F4.imprint","IMPRINT",EDGE,{"derivedFrom":subQ0}),1.0]])]});}
            var Q49;
            {var subQ0=sQuery(id+"F4.wireOp",EDGE,"E21.56.1");Q49=makeQuery(id+"F4.imprint","IMPRINT",FACE,{"disambiguationData":[TD([[makeQuery(id+"F4.imprint","IMPRINT",EDGE,{"derivedFrom":subQ0}),1.0]])]});}
            var Q50;
            {var subQ0=sQuery(id+"F4.wireOp",EDGE,"E21.39.1");Q50=makeQuery(id+"F4.imprint","IMPRINT",FACE,{"disambiguationData":[TD([[makeQuery(id+"F4.imprint","IMPRINT",EDGE,{"derivedFrom":subQ0}),1.0]])]});}
            var Q51;
            {var subQ0=sQuery(id+"F4.wireOp",EDGE,"E21.33.1");Q51=makeQuery(id+"F4.imprint","IMPRINT",FACE,{"disambiguationData":[TD([[makeQuery(id+"F4.imprint","IMPRINT",EDGE,{"derivedFrom":subQ0}),1.0]])]});}
            var Q52;
            {var subQ0=sQuery(id+"F4.wireOp",EDGE,"E21.21.1");Q52=makeQuery(id+"F4.imprint","IMPRINT",FACE,{"disambiguationData":[TD([[makeQuery(id+"F4.imprint","IMPRINT",EDGE,{"derivedFrom":subQ0}),1.0]])]});}
            var Q53;
            {var subQ0=sQuery(id+"F4.wireOp",EDGE,"E21.12.1");Q53=makeQuery(id+"F4.imprint","IMPRINT",FACE,{"disambiguationData":[TD([[makeQuery(id+"F4.imprint","IMPRINT",EDGE,{"derivedFrom":subQ0}),1.0]])]});}
            var Q54;
            {var subQ0=sQuery(id+"F4.wireOp",EDGE,"E21.24.1");Q54=makeQuery(id+"F4.imprint","IMPRINT",FACE,{"disambiguationData":[TD([[makeQuery(id+"F4.imprint","IMPRINT",EDGE,{"derivedFrom":subQ0}),1.0]])]});}
            var Q55;
            {var subQ0=sQuery(id+"F4.wireOp",EDGE,"E21.36.1");Q55=makeQuery(id+"F4.imprint","IMPRINT",FACE,{"disambiguationData":[TD([[makeQuery(id+"F4.imprint","IMPRINT",EDGE,{"derivedFrom":subQ0}),1.0]])]});}
            var Q56;
            {var subQ0=sQuery(id+"F4.wireOp",EDGE,"E21.3.1");Q56=makeQuery(id+"F4.imprint","IMPRINT",FACE,{"disambiguationData":[TD([[makeQuery(id+"F4.imprint","IMPRINT",EDGE,{"derivedFrom":subQ0}),1.0]])]});}
            var Q57;
            {var subQ0=sQuery(id+"F4.wireOp",EDGE,"E21.20.1");Q57=makeQuery(id+"F4.imprint","IMPRINT",FACE,{"disambiguationData":[TD([[makeQuery(id+"F4.imprint","IMPRINT",EDGE,{"derivedFrom":subQ0}),1.0]])]});}
            var Q58;
            {var subQ0=sQuery(id+"F4.wireOp",EDGE,"E21.23.1");Q58=makeQuery(id+"F4.imprint","IMPRINT",FACE,{"disambiguationData":[TD([[makeQuery(id+"F4.imprint","IMPRINT",EDGE,{"derivedFrom":subQ0}),1.0]])]});}
            var Q59;
            {var subQ0=sQuery(id+"F4.wireOp",EDGE,"E21.48.1");Q59=makeQuery(id+"F4.imprint","IMPRINT",FACE,{"disambiguationData":[TD([[makeQuery(id+"F4.imprint","IMPRINT",EDGE,{"derivedFrom":subQ0}),1.0]])]});}
            var Q60;
            {var subQ0=sQuery(id+"F4.wireOp",EDGE,"E21.42.1");Q60=makeQuery(id+"F4.imprint","IMPRINT",FACE,{"disambiguationData":[TD([[makeQuery(id+"F4.imprint","IMPRINT",EDGE,{"derivedFrom":subQ0}),1.0]])]});}
            var Q61;
            {var subQ0=sQuery(id+"F4.wireOp",EDGE,"E21.13.1");Q61=makeQuery(id+"F4.imprint","IMPRINT",FACE,{"disambiguationData":[TD([[makeQuery(id+"F4.imprint","IMPRINT",EDGE,{"derivedFrom":subQ0}),1.0]])]});}
            extrude(context, id + "F5", {"entities" : qUnion([Q0, Q1, Q2, Q3, Q4, Q5, Q6, Q7, Q8, Q9, Q10, Q11, Q12, Q13, Q14, Q15, Q16, Q17, Q18, Q19, Q20, Q21, Q22, Q23, Q24, Q25, Q26, Q27, Q28, Q29, Q30, Q31, Q32, Q33, Q34, Q35, Q36, Q37, Q38, Q39, Q40, Q41, Q42, Q43, Q44, Q45, Q46, Q47, Q48, Q49, Q50, Q51, Q52, Q53, Q54, Q55, Q56, Q57, Q58, Q59, Q60, Q61]), "depth" : 6 * mm, "offsetDistance" : 25 * mm});
        }
        {
            var Q0;
            Q0=makeQuery(id+"F5.opExtrude","CAP_FACE",FACE,{"disambiguationData":[OSD([sQuery(id+"F4.wireOp",EDGE,"E12"),sQuery(id+"F4.wireOp",EDGE,"E17"),sQuery(id+"F4.wireOp",EDGE,"E19.trimOffspring"),sQuery(id+"F4.wireOp",EDGE,"E20.MirrorCS"),sQuery(id+"F4.wireOp",EDGE,"E21.1.0"),sQuery(id+"F4.wireOp",EDGE,"E21.1.1"),sQuery(id+"F4.wireOp",EDGE,"E21.2.0"),sQuery(id+"F4.wireOp",EDGE,"E21.2.1"),sQuery(id+"F4.wireOp",EDGE,"E21.3.0"),sQuery(id+"F4.wireOp",EDGE,"E21.3.1"),sQuery(id+"F4.wireOp",EDGE,"E21.4.0"),sQuery(id+"F4.wireOp",EDGE,"E21.4.1"),sQuery(id+"F4.wireOp",EDGE,"E21.5.0"),sQuery(id+"F4.wireOp",EDGE,"E21.5.1"),sQuery(id+"F4.wireOp",EDGE,"E21.6.0"),sQuery(id+"F4.wireOp",EDGE,"E21.6.1"),sQuery(id+"F4.wireOp",EDGE,"E21.7.0"),sQuery(id+"F4.wireOp",EDGE,"E21.7.1"),sQuery(id+"F4.wireOp",EDGE,"E21.8.0"),sQuery(id+"F4.wireOp",EDGE,"E21.8.1"),sQuery(id+"F4.wireOp",EDGE,"E21.9.0"),sQuery(id+"F4.wireOp",EDGE,"E21.9.1"),sQuery(id+"F4.wireOp",EDGE,"E21.10.0"),sQuery(id+"F4.wireOp",EDGE,"E21.10.1"),sQuery(id+"F4.wireOp",EDGE,"E21.11.0"),sQuery(id+"F4.wireOp",EDGE,"E21.11.1"),sQuery(id+"F4.wireOp",EDGE,"E21.12.0"),sQuery(id+"F4.wireOp",EDGE,"E21.12.1"),sQuery(id+"F4.wireOp",EDGE,"E21.13.0"),sQuery(id+"F4.wireOp",EDGE,"E21.13.1"),sQuery(id+"F4.wireOp",EDGE,"E21.14.0"),sQuery(id+"F4.wireOp",EDGE,"E21.14.1"),sQuery(id+"F4.wireOp",EDGE,"E21.15.0"),sQuery(id+"F4.wireOp",EDGE,"E21.15.1"),sQuery(id+"F4.wireOp",EDGE,"E21.16.0"),sQuery(id+"F4.wireOp",EDGE,"E21.16.1"),sQuery(id+"F4.wireOp",EDGE,"E21.17.0"),sQuery(id+"F4.wireOp",EDGE,"E21.17.1"),sQuery(id+"F4.wireOp",EDGE,"E21.18.0"),sQuery(id+"F4.wireOp",EDGE,"E21.18.1"),sQuery(id+"F4.wireOp",EDGE,"E21.19.0"),sQuery(id+"F4.wireOp",EDGE,"E21.19.1"),sQuery(id+"F4.wireOp",EDGE,"E21.20.0"),sQuery(id+"F4.wireOp",EDGE,"E21.20.1"),sQuery(id+"F4.wireOp",EDGE,"E21.21.0"),sQuery(id+"F4.wireOp",EDGE,"E21.21.1"),sQuery(id+"F4.wireOp",EDGE,"E21.22.0"),sQuery(id+"F4.wireOp",EDGE,"E21.22.1"),sQuery(id+"F4.wireOp",EDGE,"E21.23.0"),sQuery(id+"F4.wireOp",EDGE,"E21.23.1"),sQuery(id+"F4.wireOp",EDGE,"E21.24.0"),sQuery(id+"F4.wireOp",EDGE,"E21.24.1"),sQuery(id+"F4.wireOp",EDGE,"E21.25.0"),sQuery(id+"F4.wireOp",EDGE,"E21.25.1"),sQuery(id+"F4.wireOp",EDGE,"E21.26.0"),sQuery(id+"F4.wireOp",EDGE,"E21.26.1"),sQuery(id+"F4.wireOp",EDGE,"E21.27.0"),sQuery(id+"F4.wireOp",EDGE,"E21.27.1"),sQuery(id+"F4.wireOp",EDGE,"E21.28.0"),sQuery(id+"F4.wireOp",EDGE,"E21.28.1"),sQuery(id+"F4.wireOp",EDGE,"E21.29.0"),sQuery(id+"F4.wireOp",EDGE,"E21.29.1"),sQuery(id+"F4.wireOp",EDGE,"E21.30.0"),sQuery(id+"F4.wireOp",EDGE,"E21.30.1"),sQuery(id+"F4.wireOp",EDGE,"E21.31.0"),sQuery(id+"F4.wireOp",EDGE,"E21.31.1"),sQuery(id+"F4.wireOp",EDGE,"E21.32.0"),sQuery(id+"F4.wireOp",EDGE,"E21.32.1"),sQuery(id+"F4.wireOp",EDGE,"E21.33.0"),sQuery(id+"F4.wireOp",EDGE,"E21.33.1"),sQuery(id+"F4.wireOp",EDGE,"E21.34.0"),sQuery(id+"F4.wireOp",EDGE,"E21.34.1"),sQuery(id+"F4.wireOp",EDGE,"E21.35.0"),sQuery(id+"F4.wireOp",EDGE,"E21.35.1"),sQuery(id+"F4.wireOp",EDGE,"E21.36.0"),sQuery(id+"F4.wireOp",EDGE,"E21.36.1"),sQuery(id+"F4.wireOp",EDGE,"E21.37.0"),sQuery(id+"F4.wireOp",EDGE,"E21.37.1"),sQuery(id+"F4.wireOp",EDGE,"E21.38.0"),sQuery(id+"F4.wireOp",EDGE,"E21.38.1"),sQuery(id+"F4.wireOp",EDGE,"E21.39.0"),sQuery(id+"F4.wireOp",EDGE,"E21.39.1"),sQuery(id+"F4.wireOp",EDGE,"E21.40.0"),sQuery(id+"F4.wireOp",EDGE,"E21.40.1"),sQuery(id+"F4.wireOp",EDGE,"E21.41.0"),sQuery(id+"F4.wireOp",EDGE,"E21.41.1"),sQuery(id+"F4.wireOp",EDGE,"E21.42.0"),sQuery(id+"F4.wireOp",EDGE,"E21.42.1"),sQuery(id+"F4.wireOp",EDGE,"E21.43.0"),sQuery(id+"F4.wireOp",EDGE,"E21.43.1"),sQuery(id+"F4.wireOp",EDGE,"E21.44.0"),sQuery(id+"F4.wireOp",EDGE,"E21.44.1"),sQuery(id+"F4.wireOp",EDGE,"E21.45.0"),sQuery(id+"F4.wireOp",EDGE,"E21.45.1"),sQuery(id+"F4.wireOp",EDGE,"E21.46.0"),sQuery(id+"F4.wireOp",EDGE,"E21.46.1"),sQuery(id+"F4.wireOp",EDGE,"E21.47.0"),sQuery(id+"F4.wireOp",EDGE,"E21.47.1"),sQuery(id+"F4.wireOp",EDGE,"E21.48.0"),sQuery(id+"F4.wireOp",EDGE,"E21.48.1"),sQuery(id+"F4.wireOp",EDGE,"E21.49.0"),sQuery(id+"F4.wireOp",EDGE,"E21.49.1"),sQuery(id+"F4.wireOp",EDGE,"E21.50.0"),sQuery(id+"F4.wireOp",EDGE,"E21.50.1"),sQuery(id+"F4.wireOp",EDGE,"E21.51.0"),sQuery(id+"F4.wireOp",EDGE,"E21.51.1"),sQuery(id+"F4.wireOp",EDGE,"E21.52.0"),sQuery(id+"F4.wireOp",EDGE,"E21.52.1"),sQuery(id+"F4.wireOp",EDGE,"E21.53.0"),sQuery(id+"F4.wireOp",EDGE,"E21.53.1"),sQuery(id+"F4.wireOp",EDGE,"E21.54.0"),sQuery(id+"F4.wireOp",EDGE,"E21.54.1"),sQuery(id+"F4.wireOp",EDGE,"E21.55.0"),sQuery(id+"F4.wireOp",EDGE,"E21.55.1"),sQuery(id+"F4.wireOp",EDGE,"E21.56.0"),sQuery(id+"F4.wireOp",EDGE,"E21.56.1"),sQuery(id+"F4.wireOp",EDGE,"E21.57.0"),sQuery(id+"F4.wireOp",EDGE,"E21.57.1"),sQuery(id+"F4.wireOp",EDGE,"E21.58.0"),sQuery(id+"F4.wireOp",EDGE,"E21.58.1"),sQuery(id+"F4.wireOp",EDGE,"E21.59.0"),sQuery(id+"F4.wireOp",EDGE,"E21.59.1"),sQuery(id+"F4.wireOp",EDGE,"E22")])],"isStart":true});
            var sketch = newSketch(context, id + "F6", { "sketchPlane" : qUnion([Q0])});
            skCircle(sketch, "E23", {"center": v(45.2, 0) * mm, "radius": 4 * mm});
            skSolve(sketch);
        }
        {
            var Q0;
            Q0 = qSketchRegion(id + "F6", true);
            extrude(context, id + "F7", {"entities" : qUnion([Q0]), "operationType" : NewBodyOperationType.REMOVE, "endBound" : BoundingType.THROUGH_ALL, "oppositeDirection" : true, "depth" : 25 * mm, "offsetDistance" : 25 * mm});
        }
        {
            var Q0;
            Q0=makeQuery(id+"F1.opExtrude","CAP_FACE",FACE,{"disambiguationData":[OSD([sQuery(id+"F0.wireOp",EDGE,"E1"),sQuery(id+"F0.wireOp",EDGE,"E2"),sQuery(id+"F0.wireOp",EDGE,"E4"),sQuery(id+"F0.wireOp",EDGE,"E6.trimOffspring"),sQuery(id+"F0.wireOp",EDGE,"E7.MirrorCS"),sQuery(id+"F0.wireOp",EDGE,"E8.1.0"),sQuery(id+"F0.wireOp",EDGE,"E8.1.1"),sQuery(id+"F0.wireOp",EDGE,"E8.2.0"),sQuery(id+"F0.wireOp",EDGE,"E8.2.1"),sQuery(id+"F0.wireOp",EDGE,"E9.1.3.0"),sQuery(id+"F0.wireOp",EDGE,"E9.4.3.0"),sQuery(id+"F0.wireOp",EDGE,"E9.1.4.0"),sQuery(id+"F0.wireOp",EDGE,"E9.4.4.0"),sQuery(id+"F0.wireOp",EDGE,"E9.1.5.0"),sQuery(id+"F0.wireOp",EDGE,"E9.4.5.0"),sQuery(id+"F0.wireOp",EDGE,"E9.1.6.0"),sQuery(id+"F0.wireOp",EDGE,"E9.4.6.0"),sQuery(id+"F0.wireOp",EDGE,"E9.1.7.0"),sQuery(id+"F0.wireOp",EDGE,"E9.4.7.0"),sQuery(id+"F0.wireOp",EDGE,"E9.1.8.0"),sQuery(id+"F0.wireOp",EDGE,"E9.4.8.0"),sQuery(id+"F0.wireOp",EDGE,"E9.1.9.0"),sQuery(id+"F0.wireOp",EDGE,"E9.4.9.0"),sQuery(id+"F0.wireOp",EDGE,"E9.1.10.0"),sQuery(id+"F0.wireOp",EDGE,"E9.4.10.0"),sQuery(id+"F0.wireOp",EDGE,"E9.1.11.0"),sQuery(id+"F0.wireOp",EDGE,"E9.4.11.0"),sQuery(id+"F0.wireOp",EDGE,"E9.1.12.0"),sQuery(id+"F0.wireOp",EDGE,"E9.4.12.0"),sQuery(id+"F0.wireOp",EDGE,"E9.1.13.0"),sQuery(id+"F0.wireOp",EDGE,"E9.4.13.0"),sQuery(id+"F0.wireOp",EDGE,"E9.1.14.0"),sQuery(id+"F0.wireOp",EDGE,"E9.4.14.0"),sQuery(id+"F0.wireOp",EDGE,"E9.1.15.0"),sQuery(id+"F0.wireOp",EDGE,"E9.4.15.0"),sQuery(id+"F0.wireOp",EDGE,"E9.1.16.0"),sQuery(id+"F0.wireOp",EDGE,"E9.4.16.0"),sQuery(id+"F0.wireOp",EDGE,"E9.1.17.0"),sQuery(id+"F0.wireOp",EDGE,"E9.4.17.0"),sQuery(id+"F0.wireOp",EDGE,"E9.1.18.0"),sQuery(id+"F0.wireOp",EDGE,"E9.4.18.0"),sQuery(id+"F0.wireOp",EDGE,"E9.1.19.0"),sQuery(id+"F0.wireOp",EDGE,"E9.4.19.0"),sQuery(id+"F0.wireOp",EDGE,"E9.1.20.0"),sQuery(id+"F0.wireOp",EDGE,"E9.4.20.0"),sQuery(id+"F0.wireOp",EDGE,"E9.1.21.0"),sQuery(id+"F0.wireOp",EDGE,"E9.4.21.0"),sQuery(id+"F0.wireOp",EDGE,"E9.1.22.0"),sQuery(id+"F0.wireOp",EDGE,"E9.4.22.0"),sQuery(id+"F0.wireOp",EDGE,"E9.1.23.0"),sQuery(id+"F0.wireOp",EDGE,"E9.4.23.0"),sQuery(id+"F0.wireOp",EDGE,"E9.1.24.0"),sQuery(id+"F0.wireOp",EDGE,"E9.4.24.0"),sQuery(id+"F0.wireOp",EDGE,"E9.1.25.0"),sQuery(id+"F0.wireOp",EDGE,"E9.4.25.0"),sQuery(id+"F0.wireOp",EDGE,"E9.1.26.0"),sQuery(id+"F0.wireOp",EDGE,"E9.4.26.0"),sQuery(id+"F0.wireOp",EDGE,"E9.1.27.0"),sQuery(id+"F0.wireOp",EDGE,"E9.4.27.0"),sQuery(id+"F0.wireOp",EDGE,"E9.1.28.0"),sQuery(id+"F0.wireOp",EDGE,"E9.4.28.0"),sQuery(id+"F0.wireOp",EDGE,"E9.1.29.0"),sQuery(id+"F0.wireOp",EDGE,"E9.4.29.0")])],"isStart":false});
            var sketch = newSketch(context, id + "F8", { "sketchPlane" : qUnion([Q0])});
            skCircle(sketch, "E24", {"center": v(7.5, 0) * mm, "radius": 1.5 * mm});
            skCircle(sketch, "E25", {"center": v(37.7, 0) * mm, "radius": 1.5 * mm});
            skPoint(sketch, "E26.start.orphan", {"position": v(0, 0) * mm});
            skPoint(sketch, "E27.end.orphan", {"position": v(45.2, 0) * mm});
            skSolve(sketch);
        }
        {
            var Q0;
            Q0=makeQuery(id+"F8.imprint","IMPRINT",FACE,{"disambiguationData":[TD([[makeQuery(id+"F8.imprint","IMPRINT",EDGE,{"derivedFrom":sQuery(id+"F8.wireOp",EDGE,"E25")}),1.0]])]});
            var Q1;
            Q1=makeQuery(id+"F8.imprint","IMPRINT",FACE,{"disambiguationData":[TD([[makeQuery(id+"F8.imprint","IMPRINT",EDGE,{"derivedFrom":sQuery(id+"F8.wireOp",EDGE,"E24")}),1.0]])]});
            extrude(context, id + "F9", {"entities" : qUnion([Q0, Q1]), "operationType" : NewBodyOperationType.REMOVE, "endBound" : BoundingType.THROUGH_ALL, "oppositeDirection" : true, "depth" : 25 * mm, "offsetDistance" : 25 * mm});
        }
        {
            var Q0;
            Q0=makeQuery(id+"F1.opExtrude","CAP_FACE",FACE,{"disambiguationData":[OSD([sQuery(id+"F0.wireOp",EDGE,"E1"),sQuery(id+"F0.wireOp",EDGE,"E2"),sQuery(id+"F0.wireOp",EDGE,"E4"),sQuery(id+"F0.wireOp",EDGE,"E6.trimOffspring"),sQuery(id+"F0.wireOp",EDGE,"E7.MirrorCS"),sQuery(id+"F0.wireOp",EDGE,"E8.1.0"),sQuery(id+"F0.wireOp",EDGE,"E8.1.1"),sQuery(id+"F0.wireOp",EDGE,"E8.2.0"),sQuery(id+"F0.wireOp",EDGE,"E8.2.1"),sQuery(id+"F0.wireOp",EDGE,"E9.1.3.0"),sQuery(id+"F0.wireOp",EDGE,"E9.4.3.0"),sQuery(id+"F0.wireOp",EDGE,"E9.1.4.0"),sQuery(id+"F0.wireOp",EDGE,"E9.4.4.0"),sQuery(id+"F0.wireOp",EDGE,"E9.1.5.0"),sQuery(id+"F0.wireOp",EDGE,"E9.4.5.0"),sQuery(id+"F0.wireOp",EDGE,"E9.1.6.0"),sQuery(id+"F0.wireOp",EDGE,"E9.4.6.0"),sQuery(id+"F0.wireOp",EDGE,"E9.1.7.0"),sQuery(id+"F0.wireOp",EDGE,"E9.4.7.0"),sQuery(id+"F0.wireOp",EDGE,"E9.1.8.0"),sQuery(id+"F0.wireOp",EDGE,"E9.4.8.0"),sQuery(id+"F0.wireOp",EDGE,"E9.1.9.0"),sQuery(id+"F0.wireOp",EDGE,"E9.4.9.0"),sQuery(id+"F0.wireOp",EDGE,"E9.1.10.0"),sQuery(id+"F0.wireOp",EDGE,"E9.4.10.0"),sQuery(id+"F0.wireOp",EDGE,"E9.1.11.0"),sQuery(id+"F0.wireOp",EDGE,"E9.4.11.0"),sQuery(id+"F0.wireOp",EDGE,"E9.1.12.0"),sQuery(id+"F0.wireOp",EDGE,"E9.4.12.0"),sQuery(id+"F0.wireOp",EDGE,"E9.1.13.0"),sQuery(id+"F0.wireOp",EDGE,"E9.4.13.0"),sQuery(id+"F0.wireOp",EDGE,"E9.1.14.0"),sQuery(id+"F0.wireOp",EDGE,"E9.4.14.0"),sQuery(id+"F0.wireOp",EDGE,"E9.1.15.0"),sQuery(id+"F0.wireOp",EDGE,"E9.4.15.0"),sQuery(id+"F0.wireOp",EDGE,"E9.1.16.0"),sQuery(id+"F0.wireOp",EDGE,"E9.4.16.0"),sQuery(id+"F0.wireOp",EDGE,"E9.1.17.0"),sQuery(id+"F0.wireOp",EDGE,"E9.4.17.0"),sQuery(id+"F0.wireOp",EDGE,"E9.1.18.0"),sQuery(id+"F0.wireOp",EDGE,"E9.4.18.0"),sQuery(id+"F0.wireOp",EDGE,"E9.1.19.0"),sQuery(id+"F0.wireOp",EDGE,"E9.4.19.0"),sQuery(id+"F0.wireOp",EDGE,"E9.1.20.0"),sQuery(id+"F0.wireOp",EDGE,"E9.4.20.0"),sQuery(id+"F0.wireOp",EDGE,"E9.1.21.0"),sQuery(id+"F0.wireOp",EDGE,"E9.4.21.0"),sQuery(id+"F0.wireOp",EDGE,"E9.1.22.0"),sQuery(id+"F0.wireOp",EDGE,"E9.4.22.0"),sQuery(id+"F0.wireOp",EDGE,"E9.1.23.0"),sQuery(id+"F0.wireOp",EDGE,"E9.4.23.0"),sQuery(id+"F0.wireOp",EDGE,"E9.1.24.0"),sQuery(id+"F0.wireOp",EDGE,"E9.4.24.0"),sQuery(id+"F0.wireOp",EDGE,"E9.1.25.0"),sQuery(id+"F0.wireOp",EDGE,"E9.4.25.0"),sQuery(id+"F0.wireOp",EDGE,"E9.1.26.0"),sQuery(id+"F0.wireOp",EDGE,"E9.4.26.0"),sQuery(id+"F0.wireOp",EDGE,"E9.1.27.0"),sQuery(id+"F0.wireOp",EDGE,"E9.4.27.0"),sQuery(id+"F0.wireOp",EDGE,"E9.1.28.0"),sQuery(id+"F0.wireOp",EDGE,"E9.4.28.0"),sQuery(id+"F0.wireOp",EDGE,"E9.1.29.0"),sQuery(id+"F0.wireOp",EDGE,"E9.4.29.0")])],"isStart":false});
            var sketch = newSketch(context, id + "F10", { "sketchPlane" : qUnion([Q0])});
            skCircle(sketch, "E28", {"center": v(7.5, 0) * mm, "radius": 1.5 * mm});
            skSolve(sketch);
        }
        {
            var Q0;
            Q0=makeQuery(id+"F10.imprint","IMPRINT",FACE,{"disambiguationData":[TD([[makeQuery(id+"F10.imprint","IMPRINT",EDGE,{"derivedFrom":sQuery(id+"F10.wireOp",EDGE,"E28")}),1.0]])]});
            extrude(context, id + "F11", {"entities" : qUnion([Q0]), "operationType" : NewBodyOperationType.REMOVE, "endBound" : BoundingType.THROUGH_ALL, "oppositeDirection" : true, "depth" : 25 * mm, "offsetDistance" : 25 * mm});
        }
        {
            var Q0;
            {var subQ0=sQuery(id+"F0.wireOp",EDGE,"E1");Q0=makeQuery(id+"F1.opExtrude","SWEPT_FACE",FACE,{"disambiguationData":[OSD([subQ0]),TDD([makeQuery(id+"F0.imprint","IMPRINT",EDGE,{"disambiguationData":[TD([[makeQuery(id+"F0.imprint","INTERSECT",VERTEX,{"derivedFrom":[subQ0,sQuery(id+"F0.wireOp",EDGE,"E9.1.9.0")]}),-1.0]])],"derivedFrom":subQ0})])]});}
            var Q1;
            {var subQ0=sQuery(id+"F0.wireOp",EDGE,"E1");Q1=makeQuery(id+"F1.opExtrude","SWEPT_FACE",FACE,{"disambiguationData":[OSD([subQ0]),TDD([makeQuery(id+"F0.imprint","IMPRINT",EDGE,{"disambiguationData":[TD([[makeQuery(id+"F0.imprint","INTERSECT",VERTEX,{"derivedFrom":[subQ0,sQuery(id+"F0.wireOp",EDGE,"E9.1.13.0")]}),-1.0]])],"derivedFrom":subQ0})])]});}
            var Q2;
            {var subQ0=sQuery(id+"F0.wireOp",EDGE,"E1");Q2=makeQuery(id+"F1.opExtrude","SWEPT_FACE",FACE,{"disambiguationData":[OSD([subQ0]),TDD([makeQuery(id+"F0.imprint","IMPRINT",EDGE,{"disambiguationData":[TD([[makeQuery(id+"F0.imprint","INTERSECT",VERTEX,{"derivedFrom":[subQ0,sQuery(id+"F0.wireOp",EDGE,"E9.1.17.0")]}),-1.0]])],"derivedFrom":subQ0})])]});}
            var Q3;
            {var subQ0=sQuery(id+"F0.wireOp",EDGE,"E1");Q3=makeQuery(id+"F1.opExtrude","SWEPT_FACE",FACE,{"disambiguationData":[OSD([subQ0]),TDD([makeQuery(id+"F0.imprint","IMPRINT",EDGE,{"disambiguationData":[TD([[makeQuery(id+"F0.imprint","INTERSECT",VERTEX,{"derivedFrom":[subQ0,sQuery(id+"F0.wireOp",EDGE,"E9.1.24.0")]}),-1.0]])],"derivedFrom":subQ0})])]});}
            var Q4;
            {var subQ0=sQuery(id+"F0.wireOp",EDGE,"E1");Q4=makeQuery(id+"F1.opExtrude","SWEPT_FACE",FACE,{"disambiguationData":[OSD([subQ0]),TDD([makeQuery(id+"F0.imprint","IMPRINT",EDGE,{"disambiguationData":[TD([[makeQuery(id+"F0.imprint","INTERSECT",VERTEX,{"derivedFrom":[subQ0,sQuery(id+"F0.wireOp",EDGE,"E9.1.22.0")]}),-1.0]])],"derivedFrom":subQ0})])]});}
            var Q5;
            {var subQ0=sQuery(id+"F0.wireOp",EDGE,"E1");Q5=makeQuery(id+"F1.opExtrude","SWEPT_FACE",FACE,{"disambiguationData":[OSD([subQ0]),TDD([makeQuery(id+"F0.imprint","IMPRINT",EDGE,{"disambiguationData":[TD([[makeQuery(id+"F0.imprint","INTERSECT",VERTEX,{"derivedFrom":[subQ0,sQuery(id+"F0.wireOp",EDGE,"E9.1.5.0")]}),-1.0]])],"derivedFrom":subQ0})])]});}
            var Q6;
            {var subQ0=sQuery(id+"F0.wireOp",EDGE,"E1");Q6=makeQuery(id+"F1.opExtrude","SWEPT_FACE",FACE,{"disambiguationData":[OSD([subQ0]),TDD([makeQuery(id+"F0.imprint","IMPRINT",EDGE,{"disambiguationData":[TD([[makeQuery(id+"F0.imprint","INTERSECT",VERTEX,{"derivedFrom":[subQ0,sQuery(id+"F0.wireOp",EDGE,"E9.1.10.0")]}),-1.0]])],"derivedFrom":subQ0})])]});}
            var Q7;
            {var subQ0=sQuery(id+"F0.wireOp",EDGE,"E1");Q7=makeQuery(id+"F1.opExtrude","SWEPT_FACE",FACE,{"disambiguationData":[OSD([subQ0]),TDD([makeQuery(id+"F0.imprint","IMPRINT",EDGE,{"disambiguationData":[TD([[makeQuery(id+"F0.imprint","INTERSECT",VERTEX,{"derivedFrom":[subQ0,sQuery(id+"F0.wireOp",EDGE,"E9.1.4.0")]}),-1.0]])],"derivedFrom":subQ0})])]});}
            var Q8;
            {var subQ0=sQuery(id+"F0.wireOp",EDGE,"E1");Q8=makeQuery(id+"F1.opExtrude","SWEPT_FACE",FACE,{"disambiguationData":[OSD([subQ0]),TDD([makeQuery(id+"F0.imprint","IMPRINT",EDGE,{"disambiguationData":[TD([[makeQuery(id+"F0.imprint","INTERSECT",VERTEX,{"derivedFrom":[subQ0,sQuery(id+"F0.wireOp",EDGE,"E8.2.0")]}),-1.0]])],"derivedFrom":subQ0})])]});}
            var Q9;
            {var subQ0=sQuery(id+"F0.wireOp",EDGE,"E1");Q9=makeQuery(id+"F1.opExtrude","SWEPT_FACE",FACE,{"disambiguationData":[OSD([subQ0]),TDD([makeQuery(id+"F0.imprint","IMPRINT",EDGE,{"disambiguationData":[TD([[makeQuery(id+"F0.imprint","INTERSECT",VERTEX,{"derivedFrom":[subQ0,sQuery(id+"F0.wireOp",EDGE,"E9.1.15.0")]}),-1.0]])],"derivedFrom":subQ0})])]});}
            var Q10;
            {var subQ0=sQuery(id+"F0.wireOp",EDGE,"E1");Q10=makeQuery(id+"F1.opExtrude","SWEPT_FACE",FACE,{"disambiguationData":[OSD([subQ0]),TDD([makeQuery(id+"F0.imprint","IMPRINT",EDGE,{"disambiguationData":[TD([[makeQuery(id+"F0.imprint","INTERSECT",VERTEX,{"derivedFrom":[subQ0,sQuery(id+"F0.wireOp",EDGE,"E9.1.16.0")]}),-1.0]])],"derivedFrom":subQ0})])]});}
            var Q11;
            {var subQ0=sQuery(id+"F0.wireOp",EDGE,"E1");Q11=makeQuery(id+"F1.opExtrude","SWEPT_FACE",FACE,{"disambiguationData":[OSD([subQ0]),TDD([makeQuery(id+"F0.imprint","IMPRINT",EDGE,{"disambiguationData":[TD([[makeQuery(id+"F0.imprint","INTERSECT",VERTEX,{"derivedFrom":[subQ0,sQuery(id+"F0.wireOp",EDGE,"E9.1.6.0")]}),-1.0]])],"derivedFrom":subQ0})])]});}
            var Q12;
            {var subQ0=sQuery(id+"F0.wireOp",EDGE,"E1");Q12=makeQuery(id+"F1.opExtrude","SWEPT_FACE",FACE,{"disambiguationData":[OSD([subQ0]),TDD([makeQuery(id+"F0.imprint","IMPRINT",EDGE,{"disambiguationData":[TD([[makeQuery(id+"F0.imprint","INTERSECT",VERTEX,{"derivedFrom":[subQ0,sQuery(id+"F0.wireOp",EDGE,"E8.1.0")]}),-1.0]])],"derivedFrom":subQ0})])]});}
            var Q13;
            {var subQ0=sQuery(id+"F0.wireOp",EDGE,"E1");Q13=makeQuery(id+"F1.opExtrude","SWEPT_FACE",FACE,{"disambiguationData":[OSD([subQ0]),TDD([makeQuery(id+"F0.imprint","IMPRINT",EDGE,{"disambiguationData":[TD([[makeQuery(id+"F0.imprint","INTERSECT",VERTEX,{"derivedFrom":[subQ0,sQuery(id+"F0.wireOp",EDGE,"E9.1.11.0")]}),-1.0]])],"derivedFrom":subQ0})])]});}
            var Q14;
            {var subQ0=sQuery(id+"F0.wireOp",EDGE,"E1");Q14=makeQuery(id+"F1.opExtrude","SWEPT_FACE",FACE,{"disambiguationData":[OSD([subQ0]),TDD([makeQuery(id+"F0.imprint","IMPRINT",EDGE,{"disambiguationData":[TD([[makeQuery(id+"F0.imprint","INTERSECT",VERTEX,{"derivedFrom":[subQ0,sQuery(id+"F0.wireOp",EDGE,"E9.1.23.0")]}),-1.0]])],"derivedFrom":subQ0})])]});}
            var Q15;
            {var subQ0=sQuery(id+"F0.wireOp",EDGE,"E1");Q15=makeQuery(id+"F1.opExtrude","SWEPT_FACE",FACE,{"disambiguationData":[OSD([subQ0]),TDD([makeQuery(id+"F0.imprint","IMPRINT",EDGE,{"disambiguationData":[TD([[makeQuery(id+"F0.imprint","INTERSECT",VERTEX,{"derivedFrom":[subQ0,sQuery(id+"F0.wireOp",EDGE,"E6.trimOffspring")]}),-1.0]])],"derivedFrom":subQ0})])]});}
            var Q16;
            {var subQ0=sQuery(id+"F0.wireOp",EDGE,"E1");Q16=makeQuery(id+"F1.opExtrude","SWEPT_FACE",FACE,{"disambiguationData":[OSD([subQ0]),TDD([makeQuery(id+"F0.imprint","IMPRINT",EDGE,{"disambiguationData":[TD([[makeQuery(id+"F0.imprint","INTERSECT",VERTEX,{"derivedFrom":[subQ0,sQuery(id+"F0.wireOp",EDGE,"E9.1.20.0")]}),-1.0]])],"derivedFrom":subQ0})])]});}
            var Q17;
            {var subQ0=sQuery(id+"F0.wireOp",EDGE,"E1");Q17=makeQuery(id+"F1.opExtrude","SWEPT_FACE",FACE,{"disambiguationData":[OSD([subQ0]),TDD([makeQuery(id+"F0.imprint","IMPRINT",EDGE,{"disambiguationData":[TD([[makeQuery(id+"F0.imprint","INTERSECT",VERTEX,{"derivedFrom":[subQ0,sQuery(id+"F0.wireOp",EDGE,"E9.1.7.0")]}),-1.0]])],"derivedFrom":subQ0})])]});}
            var Q18;
            {var subQ0=sQuery(id+"F0.wireOp",EDGE,"E1");Q18=makeQuery(id+"F1.opExtrude","SWEPT_FACE",FACE,{"disambiguationData":[OSD([subQ0]),TDD([makeQuery(id+"F0.imprint","IMPRINT",EDGE,{"disambiguationData":[TD([[makeQuery(id+"F0.imprint","INTERSECT",VERTEX,{"derivedFrom":[subQ0,sQuery(id+"F0.wireOp",EDGE,"E9.1.18.0")]}),-1.0]])],"derivedFrom":subQ0})])]});}
            var Q19;
            {var subQ0=sQuery(id+"F0.wireOp",EDGE,"E1");Q19=makeQuery(id+"F1.opExtrude","SWEPT_FACE",FACE,{"disambiguationData":[OSD([subQ0]),TDD([makeQuery(id+"F0.imprint","IMPRINT",EDGE,{"disambiguationData":[TD([[makeQuery(id+"F0.imprint","INTERSECT",VERTEX,{"derivedFrom":[subQ0,sQuery(id+"F0.wireOp",EDGE,"E9.1.21.0")]}),-1.0]])],"derivedFrom":subQ0})])]});}
            var Q20;
            {var subQ0=sQuery(id+"F0.wireOp",EDGE,"E1");Q20=makeQuery(id+"F1.opExtrude","SWEPT_FACE",FACE,{"disambiguationData":[OSD([subQ0]),TDD([makeQuery(id+"F0.imprint","IMPRINT",EDGE,{"disambiguationData":[TD([[makeQuery(id+"F0.imprint","INTERSECT",VERTEX,{"derivedFrom":[subQ0,sQuery(id+"F0.wireOp",EDGE,"E9.1.25.0")]}),-1.0]])],"derivedFrom":subQ0})])]});}
            var Q21;
            {var subQ0=sQuery(id+"F0.wireOp",EDGE,"E1");Q21=makeQuery(id+"F1.opExtrude","SWEPT_FACE",FACE,{"disambiguationData":[OSD([subQ0]),TDD([makeQuery(id+"F0.imprint","IMPRINT",EDGE,{"disambiguationData":[TD([[makeQuery(id+"F0.imprint","INTERSECT",VERTEX,{"derivedFrom":[subQ0,sQuery(id+"F0.wireOp",EDGE,"E9.1.8.0")]}),-1.0]])],"derivedFrom":subQ0})])]});}
            var Q22;
            {var subQ0=sQuery(id+"F0.wireOp",EDGE,"E1");Q22=makeQuery(id+"F1.opExtrude","SWEPT_FACE",FACE,{"disambiguationData":[OSD([subQ0]),TDD([makeQuery(id+"F0.imprint","IMPRINT",EDGE,{"disambiguationData":[TD([[makeQuery(id+"F0.imprint","INTERSECT",VERTEX,{"derivedFrom":[subQ0,sQuery(id+"F0.wireOp",EDGE,"E9.1.28.0")]}),-1.0]])],"derivedFrom":subQ0})])]});}
            var Q23;
            {var subQ0=sQuery(id+"F0.wireOp",EDGE,"E1");Q23=makeQuery(id+"F1.opExtrude","SWEPT_FACE",FACE,{"disambiguationData":[OSD([subQ0]),TDD([makeQuery(id+"F0.imprint","IMPRINT",EDGE,{"disambiguationData":[TD([[makeQuery(id+"F0.imprint","INTERSECT",VERTEX,{"derivedFrom":[subQ0,sQuery(id+"F0.wireOp",EDGE,"E7.MirrorCS")]}),1.0]])],"derivedFrom":subQ0})])]});}
            var Q24;
            {var subQ0=sQuery(id+"F0.wireOp",EDGE,"E1");Q24=makeQuery(id+"F1.opExtrude","SWEPT_FACE",FACE,{"disambiguationData":[OSD([subQ0]),TDD([makeQuery(id+"F0.imprint","IMPRINT",EDGE,{"disambiguationData":[TD([[makeQuery(id+"F0.imprint","INTERSECT",VERTEX,{"derivedFrom":[subQ0,sQuery(id+"F0.wireOp",EDGE,"E9.1.26.0")]}),-1.0]])],"derivedFrom":subQ0})])]});}
            var Q25;
            {var subQ0=sQuery(id+"F0.wireOp",EDGE,"E1");Q25=makeQuery(id+"F1.opExtrude","SWEPT_FACE",FACE,{"disambiguationData":[OSD([subQ0]),TDD([makeQuery(id+"F0.imprint","IMPRINT",EDGE,{"disambiguationData":[TD([[makeQuery(id+"F0.imprint","INTERSECT",VERTEX,{"derivedFrom":[subQ0,sQuery(id+"F0.wireOp",EDGE,"E9.1.27.0")]}),-1.0]])],"derivedFrom":subQ0})])]});}
            var Q26;
            {var subQ0=sQuery(id+"F0.wireOp",EDGE,"E1");Q26=makeQuery(id+"F1.opExtrude","SWEPT_FACE",FACE,{"disambiguationData":[OSD([subQ0]),TDD([makeQuery(id+"F0.imprint","IMPRINT",EDGE,{"disambiguationData":[TD([[makeQuery(id+"F0.imprint","INTERSECT",VERTEX,{"derivedFrom":[subQ0,sQuery(id+"F0.wireOp",EDGE,"E9.1.19.0")]}),-1.0]])],"derivedFrom":subQ0})])]});}
            var Q27;
            {var subQ0=sQuery(id+"F0.wireOp",EDGE,"E1");Q27=makeQuery(id+"F1.opExtrude","SWEPT_FACE",FACE,{"disambiguationData":[OSD([subQ0]),TDD([makeQuery(id+"F0.imprint","IMPRINT",EDGE,{"disambiguationData":[TD([[makeQuery(id+"F0.imprint","INTERSECT",VERTEX,{"derivedFrom":[subQ0,sQuery(id+"F0.wireOp",EDGE,"E9.1.3.0")]}),-1.0]])],"derivedFrom":subQ0})])]});}
            var Q28;
            {var subQ0=sQuery(id+"F0.wireOp",EDGE,"E1");Q28=makeQuery(id+"F1.opExtrude","SWEPT_FACE",FACE,{"disambiguationData":[OSD([subQ0]),TDD([makeQuery(id+"F0.imprint","IMPRINT",EDGE,{"disambiguationData":[TD([[makeQuery(id+"F0.imprint","INTERSECT",VERTEX,{"derivedFrom":[subQ0,sQuery(id+"F0.wireOp",EDGE,"E9.1.12.0")]}),-1.0]])],"derivedFrom":subQ0})])]});}
            var Q29;
            {var subQ0=sQuery(id+"F0.wireOp",EDGE,"E1");Q29=makeQuery(id+"F1.opExtrude","SWEPT_FACE",FACE,{"disambiguationData":[OSD([subQ0]),TDD([makeQuery(id+"F0.imprint","IMPRINT",EDGE,{"disambiguationData":[TD([[makeQuery(id+"F0.imprint","INTERSECT",VERTEX,{"derivedFrom":[subQ0,sQuery(id+"F0.wireOp",EDGE,"E9.1.14.0")]}),-1.0]])],"derivedFrom":subQ0})])]});}
            fillet(context, id + "F12", {"entities" : qUnion([Q0, Q1, Q2, Q3, Q4, Q5, Q6, Q7, Q8, Q9, Q10, Q11, Q12, Q13, Q14, Q15, Q16, Q17, Q18, Q19, Q20, Q21, Q22, Q23, Q24, Q25, Q26, Q27, Q28, Q29]), "radius" : 0.3 * mm, "tangentPropagation" : true, "allowEdgeOverflow" : false});
        }
        {
            var Q0;
            {var subQ0=sQuery(id+"F4.wireOp",EDGE,"E12");Q0=makeQuery(id+"F5.opExtrude","SWEPT_FACE",FACE,{"disambiguationData":[OSD([subQ0]),TDD([makeQuery(id+"F4.imprint","IMPRINT",EDGE,{"disambiguationData":[TD([[makeQuery(id+"F4.imprint","INTERSECT",VERTEX,{"derivedFrom":[subQ0,sQuery(id+"F4.wireOp",EDGE,"E21.35.1")]}),-1.0]])],"derivedFrom":subQ0})])]});}
            var Q1;
            {var subQ0=sQuery(id+"F4.wireOp",EDGE,"E12");Q1=makeQuery(id+"F5.opExtrude","SWEPT_FACE",FACE,{"disambiguationData":[OSD([subQ0]),TDD([makeQuery(id+"F4.imprint","IMPRINT",EDGE,{"disambiguationData":[TD([[makeQuery(id+"F4.imprint","INTERSECT",VERTEX,{"derivedFrom":[subQ0,sQuery(id+"F4.wireOp",EDGE,"E21.39.1")]}),-1.0]])],"derivedFrom":subQ0})])]});}
            var Q2;
            {var subQ0=sQuery(id+"F4.wireOp",EDGE,"E12");Q2=makeQuery(id+"F5.opExtrude","SWEPT_FACE",FACE,{"disambiguationData":[OSD([subQ0]),TDD([makeQuery(id+"F4.imprint","IMPRINT",EDGE,{"disambiguationData":[TD([[makeQuery(id+"F4.imprint","INTERSECT",VERTEX,{"derivedFrom":[subQ0,sQuery(id+"F4.wireOp",EDGE,"E21.22.1")]}),-1.0]])],"derivedFrom":subQ0})])]});}
            var Q3;
            {var subQ0=sQuery(id+"F4.wireOp",EDGE,"E12");Q3=makeQuery(id+"F5.opExtrude","SWEPT_FACE",FACE,{"disambiguationData":[OSD([subQ0]),TDD([makeQuery(id+"F4.imprint","IMPRINT",EDGE,{"disambiguationData":[TD([[makeQuery(id+"F4.imprint","INTERSECT",VERTEX,{"derivedFrom":[subQ0,sQuery(id+"F4.wireOp",EDGE,"E19.trimOffspring")]}),-1.0]])],"derivedFrom":subQ0})])]});}
            var Q4;
            {var subQ0=sQuery(id+"F4.wireOp",EDGE,"E12");Q4=makeQuery(id+"F5.opExtrude","SWEPT_FACE",FACE,{"disambiguationData":[OSD([subQ0]),TDD([makeQuery(id+"F4.imprint","IMPRINT",EDGE,{"disambiguationData":[TD([[makeQuery(id+"F4.imprint","INTERSECT",VERTEX,{"derivedFrom":[subQ0,sQuery(id+"F4.wireOp",EDGE,"E21.50.1")]}),-1.0]])],"derivedFrom":subQ0})])]});}
            var Q5;
            {var subQ0=sQuery(id+"F4.wireOp",EDGE,"E12");Q5=makeQuery(id+"F5.opExtrude","SWEPT_FACE",FACE,{"disambiguationData":[OSD([subQ0]),TDD([makeQuery(id+"F4.imprint","IMPRINT",EDGE,{"disambiguationData":[TD([[makeQuery(id+"F4.imprint","INTERSECT",VERTEX,{"derivedFrom":[subQ0,sQuery(id+"F4.wireOp",EDGE,"E21.18.1")]}),-1.0]])],"derivedFrom":subQ0})])]});}
            var Q6;
            {var subQ0=sQuery(id+"F4.wireOp",EDGE,"E12");Q6=makeQuery(id+"F5.opExtrude","SWEPT_FACE",FACE,{"disambiguationData":[OSD([subQ0]),TDD([makeQuery(id+"F4.imprint","IMPRINT",EDGE,{"disambiguationData":[TD([[makeQuery(id+"F4.imprint","INTERSECT",VERTEX,{"derivedFrom":[subQ0,sQuery(id+"F4.wireOp",EDGE,"E21.46.1")]}),-1.0]])],"derivedFrom":subQ0})])]});}
            var Q7;
            {var subQ0=sQuery(id+"F4.wireOp",EDGE,"E12");Q7=makeQuery(id+"F5.opExtrude","SWEPT_FACE",FACE,{"disambiguationData":[OSD([subQ0]),TDD([makeQuery(id+"F4.imprint","IMPRINT",EDGE,{"disambiguationData":[TD([[makeQuery(id+"F4.imprint","INTERSECT",VERTEX,{"derivedFrom":[subQ0,sQuery(id+"F4.wireOp",EDGE,"E21.37.1")]}),-1.0]])],"derivedFrom":subQ0})])]});}
            var Q8;
            {var subQ0=sQuery(id+"F4.wireOp",EDGE,"E12");Q8=makeQuery(id+"F5.opExtrude","SWEPT_FACE",FACE,{"disambiguationData":[OSD([subQ0]),TDD([makeQuery(id+"F4.imprint","IMPRINT",EDGE,{"disambiguationData":[TD([[makeQuery(id+"F4.imprint","INTERSECT",VERTEX,{"derivedFrom":[subQ0,sQuery(id+"F4.wireOp",EDGE,"E21.55.1")]}),-1.0]])],"derivedFrom":subQ0})])]});}
            var Q9;
            {var subQ0=sQuery(id+"F4.wireOp",EDGE,"E12");Q9=makeQuery(id+"F5.opExtrude","SWEPT_FACE",FACE,{"disambiguationData":[OSD([subQ0]),TDD([makeQuery(id+"F4.imprint","IMPRINT",EDGE,{"disambiguationData":[TD([[makeQuery(id+"F4.imprint","INTERSECT",VERTEX,{"derivedFrom":[subQ0,sQuery(id+"F4.wireOp",EDGE,"E21.41.1")]}),-1.0]])],"derivedFrom":subQ0})])]});}
            var Q10;
            {var subQ0=sQuery(id+"F4.wireOp",EDGE,"E12");Q10=makeQuery(id+"F5.opExtrude","SWEPT_FACE",FACE,{"disambiguationData":[OSD([subQ0]),TDD([makeQuery(id+"F4.imprint","IMPRINT",EDGE,{"disambiguationData":[TD([[makeQuery(id+"F4.imprint","INTERSECT",VERTEX,{"derivedFrom":[subQ0,sQuery(id+"F4.wireOp",EDGE,"E21.32.1")]}),-1.0]])],"derivedFrom":subQ0})])]});}
            var Q11;
            {var subQ0=sQuery(id+"F4.wireOp",EDGE,"E12");Q11=makeQuery(id+"F5.opExtrude","SWEPT_FACE",FACE,{"disambiguationData":[OSD([subQ0]),TDD([makeQuery(id+"F4.imprint","IMPRINT",EDGE,{"disambiguationData":[TD([[makeQuery(id+"F4.imprint","INTERSECT",VERTEX,{"derivedFrom":[subQ0,sQuery(id+"F4.wireOp",EDGE,"E21.34.1")]}),-1.0]])],"derivedFrom":subQ0})])]});}
            var Q12;
            {var subQ0=sQuery(id+"F4.wireOp",EDGE,"E12");Q12=makeQuery(id+"F5.opExtrude","SWEPT_FACE",FACE,{"disambiguationData":[OSD([subQ0]),TDD([makeQuery(id+"F4.imprint","IMPRINT",EDGE,{"disambiguationData":[TD([[makeQuery(id+"F4.imprint","INTERSECT",VERTEX,{"derivedFrom":[subQ0,sQuery(id+"F4.wireOp",EDGE,"E21.25.1")]}),-1.0]])],"derivedFrom":subQ0})])]});}
            var Q13;
            {var subQ0=sQuery(id+"F4.wireOp",EDGE,"E12");Q13=makeQuery(id+"F5.opExtrude","SWEPT_FACE",FACE,{"disambiguationData":[OSD([subQ0]),TDD([makeQuery(id+"F4.imprint","IMPRINT",EDGE,{"disambiguationData":[TD([[makeQuery(id+"F4.imprint","INTERSECT",VERTEX,{"derivedFrom":[subQ0,sQuery(id+"F4.wireOp",EDGE,"E21.48.1")]}),-1.0]])],"derivedFrom":subQ0})])]});}
            var Q14;
            {var subQ0=sQuery(id+"F4.wireOp",EDGE,"E12");Q14=makeQuery(id+"F5.opExtrude","SWEPT_FACE",FACE,{"disambiguationData":[OSD([subQ0]),TDD([makeQuery(id+"F4.imprint","IMPRINT",EDGE,{"disambiguationData":[TD([[makeQuery(id+"F4.imprint","INTERSECT",VERTEX,{"derivedFrom":[subQ0,sQuery(id+"F4.wireOp",EDGE,"E21.1.1")]}),-1.0]])],"derivedFrom":subQ0})])]});}
            var Q15;
            {var subQ0=sQuery(id+"F4.wireOp",EDGE,"E12");Q15=makeQuery(id+"F5.opExtrude","SWEPT_FACE",FACE,{"disambiguationData":[OSD([subQ0]),TDD([makeQuery(id+"F4.imprint","IMPRINT",EDGE,{"disambiguationData":[TD([[makeQuery(id+"F4.imprint","INTERSECT",VERTEX,{"derivedFrom":[subQ0,sQuery(id+"F4.wireOp",EDGE,"E21.10.1")]}),-1.0]])],"derivedFrom":subQ0})])]});}
            var Q16;
            {var subQ0=sQuery(id+"F4.wireOp",EDGE,"E12");Q16=makeQuery(id+"F5.opExtrude","SWEPT_FACE",FACE,{"disambiguationData":[OSD([subQ0]),TDD([makeQuery(id+"F4.imprint","IMPRINT",EDGE,{"disambiguationData":[TD([[makeQuery(id+"F4.imprint","INTERSECT",VERTEX,{"derivedFrom":[subQ0,sQuery(id+"F4.wireOp",EDGE,"E21.9.1")]}),-1.0]])],"derivedFrom":subQ0})])]});}
            var Q17;
            {var subQ0=sQuery(id+"F4.wireOp",EDGE,"E12");Q17=makeQuery(id+"F5.opExtrude","SWEPT_FACE",FACE,{"disambiguationData":[OSD([subQ0]),TDD([makeQuery(id+"F4.imprint","IMPRINT",EDGE,{"disambiguationData":[TD([[makeQuery(id+"F4.imprint","INTERSECT",VERTEX,{"derivedFrom":[subQ0,sQuery(id+"F4.wireOp",EDGE,"E21.58.1")]}),-1.0]])],"derivedFrom":subQ0})])]});}
            var Q18;
            {var subQ0=sQuery(id+"F4.wireOp",EDGE,"E12");Q18=makeQuery(id+"F5.opExtrude","SWEPT_FACE",FACE,{"disambiguationData":[OSD([subQ0]),TDD([makeQuery(id+"F4.imprint","IMPRINT",EDGE,{"disambiguationData":[TD([[makeQuery(id+"F4.imprint","INTERSECT",VERTEX,{"derivedFrom":[subQ0,sQuery(id+"F4.wireOp",EDGE,"E21.15.1")]}),-1.0]])],"derivedFrom":subQ0})])]});}
            var Q19;
            {var subQ0=sQuery(id+"F4.wireOp",EDGE,"E12");Q19=makeQuery(id+"F5.opExtrude","SWEPT_FACE",FACE,{"disambiguationData":[OSD([subQ0]),TDD([makeQuery(id+"F4.imprint","IMPRINT",EDGE,{"disambiguationData":[TD([[makeQuery(id+"F4.imprint","INTERSECT",VERTEX,{"derivedFrom":[subQ0,sQuery(id+"F4.wireOp",EDGE,"E21.47.1")]}),-1.0]])],"derivedFrom":subQ0})])]});}
            var Q20;
            {var subQ0=sQuery(id+"F4.wireOp",EDGE,"E12");Q20=makeQuery(id+"F5.opExtrude","SWEPT_FACE",FACE,{"disambiguationData":[OSD([subQ0]),TDD([makeQuery(id+"F4.imprint","IMPRINT",EDGE,{"disambiguationData":[TD([[makeQuery(id+"F4.imprint","INTERSECT",VERTEX,{"derivedFrom":[subQ0,sQuery(id+"F4.wireOp",EDGE,"E21.33.1")]}),-1.0]])],"derivedFrom":subQ0})])]});}
            var Q21;
            {var subQ0=sQuery(id+"F4.wireOp",EDGE,"E12");Q21=makeQuery(id+"F5.opExtrude","SWEPT_FACE",FACE,{"disambiguationData":[OSD([subQ0]),TDD([makeQuery(id+"F4.imprint","IMPRINT",EDGE,{"disambiguationData":[TD([[makeQuery(id+"F4.imprint","INTERSECT",VERTEX,{"derivedFrom":[subQ0,sQuery(id+"F4.wireOp",EDGE,"E21.57.1")]}),-1.0]])],"derivedFrom":subQ0})])]});}
            var Q22;
            {var subQ0=sQuery(id+"F4.wireOp",EDGE,"E12");Q22=makeQuery(id+"F5.opExtrude","SWEPT_FACE",FACE,{"disambiguationData":[OSD([subQ0]),TDD([makeQuery(id+"F4.imprint","IMPRINT",EDGE,{"disambiguationData":[TD([[makeQuery(id+"F4.imprint","INTERSECT",VERTEX,{"derivedFrom":[subQ0,sQuery(id+"F4.wireOp",EDGE,"E21.52.1")]}),-1.0]])],"derivedFrom":subQ0})])]});}
            var Q23;
            {var subQ0=sQuery(id+"F4.wireOp",EDGE,"E12");Q23=makeQuery(id+"F5.opExtrude","SWEPT_FACE",FACE,{"disambiguationData":[OSD([subQ0]),TDD([makeQuery(id+"F4.imprint","IMPRINT",EDGE,{"disambiguationData":[TD([[makeQuery(id+"F4.imprint","INTERSECT",VERTEX,{"derivedFrom":[subQ0,sQuery(id+"F4.wireOp",EDGE,"E21.40.1")]}),-1.0]])],"derivedFrom":subQ0})])]});}
            var Q24;
            {var subQ0=sQuery(id+"F4.wireOp",EDGE,"E12");Q24=makeQuery(id+"F5.opExtrude","SWEPT_FACE",FACE,{"disambiguationData":[OSD([subQ0]),TDD([makeQuery(id+"F4.imprint","IMPRINT",EDGE,{"disambiguationData":[TD([[makeQuery(id+"F4.imprint","INTERSECT",VERTEX,{"derivedFrom":[subQ0,sQuery(id+"F4.wireOp",EDGE,"E21.5.1")]}),-1.0]])],"derivedFrom":subQ0})])]});}
            var Q25;
            {var subQ0=sQuery(id+"F4.wireOp",EDGE,"E12");Q25=makeQuery(id+"F5.opExtrude","SWEPT_FACE",FACE,{"disambiguationData":[OSD([subQ0]),TDD([makeQuery(id+"F4.imprint","IMPRINT",EDGE,{"disambiguationData":[TD([[makeQuery(id+"F4.imprint","INTERSECT",VERTEX,{"derivedFrom":[subQ0,sQuery(id+"F4.wireOp",EDGE,"E21.43.1")]}),-1.0]])],"derivedFrom":subQ0})])]});}
            var Q26;
            {var subQ0=sQuery(id+"F4.wireOp",EDGE,"E12");Q26=makeQuery(id+"F5.opExtrude","SWEPT_FACE",FACE,{"disambiguationData":[OSD([subQ0]),TDD([makeQuery(id+"F4.imprint","IMPRINT",EDGE,{"disambiguationData":[TD([[makeQuery(id+"F4.imprint","INTERSECT",VERTEX,{"derivedFrom":[subQ0,sQuery(id+"F4.wireOp",EDGE,"E21.45.1")]}),-1.0]])],"derivedFrom":subQ0})])]});}
            var Q27;
            {var subQ0=sQuery(id+"F4.wireOp",EDGE,"E12");Q27=makeQuery(id+"F5.opExtrude","SWEPT_FACE",FACE,{"disambiguationData":[OSD([subQ0]),TDD([makeQuery(id+"F4.imprint","IMPRINT",EDGE,{"disambiguationData":[TD([[makeQuery(id+"F4.imprint","INTERSECT",VERTEX,{"derivedFrom":[subQ0,sQuery(id+"F4.wireOp",EDGE,"E21.31.1")]}),-1.0]])],"derivedFrom":subQ0})])]});}
            var Q28;
            {var subQ0=sQuery(id+"F4.wireOp",EDGE,"E12");Q28=makeQuery(id+"F5.opExtrude","SWEPT_FACE",FACE,{"disambiguationData":[OSD([subQ0]),TDD([makeQuery(id+"F4.imprint","IMPRINT",EDGE,{"disambiguationData":[TD([[makeQuery(id+"F4.imprint","INTERSECT",VERTEX,{"derivedFrom":[subQ0,sQuery(id+"F4.wireOp",EDGE,"E21.2.1")]}),-1.0]])],"derivedFrom":subQ0})])]});}
            var Q29;
            {var subQ0=sQuery(id+"F4.wireOp",EDGE,"E12");Q29=makeQuery(id+"F5.opExtrude","SWEPT_FACE",FACE,{"disambiguationData":[OSD([subQ0]),TDD([makeQuery(id+"F4.imprint","IMPRINT",EDGE,{"disambiguationData":[TD([[makeQuery(id+"F4.imprint","INTERSECT",VERTEX,{"derivedFrom":[subQ0,sQuery(id+"F4.wireOp",EDGE,"E21.29.1")]}),-1.0]])],"derivedFrom":subQ0})])]});}
            var Q30;
            {var subQ0=sQuery(id+"F4.wireOp",EDGE,"E12");Q30=makeQuery(id+"F5.opExtrude","SWEPT_FACE",FACE,{"disambiguationData":[OSD([subQ0]),TDD([makeQuery(id+"F4.imprint","IMPRINT",EDGE,{"disambiguationData":[TD([[makeQuery(id+"F4.imprint","INTERSECT",VERTEX,{"derivedFrom":[subQ0,sQuery(id+"F4.wireOp",EDGE,"E21.42.1")]}),-1.0]])],"derivedFrom":subQ0})])]});}
            var Q31;
            {var subQ0=sQuery(id+"F4.wireOp",EDGE,"E12");Q31=makeQuery(id+"F5.opExtrude","SWEPT_FACE",FACE,{"disambiguationData":[OSD([subQ0]),TDD([makeQuery(id+"F4.imprint","IMPRINT",EDGE,{"disambiguationData":[TD([[makeQuery(id+"F4.imprint","INTERSECT",VERTEX,{"derivedFrom":[subQ0,sQuery(id+"F4.wireOp",EDGE,"E21.24.1")]}),-1.0]])],"derivedFrom":subQ0})])]});}
            var Q32;
            {var subQ0=sQuery(id+"F4.wireOp",EDGE,"E12");Q32=makeQuery(id+"F5.opExtrude","SWEPT_FACE",FACE,{"disambiguationData":[OSD([subQ0]),TDD([makeQuery(id+"F4.imprint","IMPRINT",EDGE,{"disambiguationData":[TD([[makeQuery(id+"F4.imprint","INTERSECT",VERTEX,{"derivedFrom":[subQ0,sQuery(id+"F4.wireOp",EDGE,"E21.27.1")]}),-1.0]])],"derivedFrom":subQ0})])]});}
            var Q33;
            {var subQ0=sQuery(id+"F4.wireOp",EDGE,"E12");Q33=makeQuery(id+"F5.opExtrude","SWEPT_FACE",FACE,{"disambiguationData":[OSD([subQ0]),TDD([makeQuery(id+"F4.imprint","IMPRINT",EDGE,{"disambiguationData":[TD([[makeQuery(id+"F4.imprint","INTERSECT",VERTEX,{"derivedFrom":[subQ0,sQuery(id+"F4.wireOp",EDGE,"E21.49.1")]}),-1.0]])],"derivedFrom":subQ0})])]});}
            var Q34;
            {var subQ0=sQuery(id+"F4.wireOp",EDGE,"E12");Q34=makeQuery(id+"F5.opExtrude","SWEPT_FACE",FACE,{"disambiguationData":[OSD([subQ0]),TDD([makeQuery(id+"F4.imprint","IMPRINT",EDGE,{"disambiguationData":[TD([[makeQuery(id+"F4.imprint","INTERSECT",VERTEX,{"derivedFrom":[subQ0,sQuery(id+"F4.wireOp",EDGE,"E21.3.1")]}),-1.0]])],"derivedFrom":subQ0})])]});}
            var Q35;
            {var subQ0=sQuery(id+"F4.wireOp",EDGE,"E12");Q35=makeQuery(id+"F5.opExtrude","SWEPT_FACE",FACE,{"disambiguationData":[OSD([subQ0]),TDD([makeQuery(id+"F4.imprint","IMPRINT",EDGE,{"disambiguationData":[TD([[makeQuery(id+"F4.imprint","INTERSECT",VERTEX,{"derivedFrom":[subQ0,sQuery(id+"F4.wireOp",EDGE,"E21.21.1")]}),-1.0]])],"derivedFrom":subQ0})])]});}
            var Q36;
            {var subQ0=sQuery(id+"F4.wireOp",EDGE,"E12");Q36=makeQuery(id+"F5.opExtrude","SWEPT_FACE",FACE,{"disambiguationData":[OSD([subQ0]),TDD([makeQuery(id+"F4.imprint","IMPRINT",EDGE,{"disambiguationData":[TD([[makeQuery(id+"F4.imprint","INTERSECT",VERTEX,{"derivedFrom":[subQ0,sQuery(id+"F4.wireOp",EDGE,"E21.28.1")]}),-1.0]])],"derivedFrom":subQ0})])]});}
            var Q37;
            {var subQ0=sQuery(id+"F4.wireOp",EDGE,"E12");Q37=makeQuery(id+"F5.opExtrude","SWEPT_FACE",FACE,{"disambiguationData":[OSD([subQ0]),TDD([makeQuery(id+"F4.imprint","IMPRINT",EDGE,{"disambiguationData":[TD([[makeQuery(id+"F4.imprint","INTERSECT",VERTEX,{"derivedFrom":[subQ0,sQuery(id+"F4.wireOp",EDGE,"E21.20.1")]}),-1.0]])],"derivedFrom":subQ0})])]});}
            var Q38;
            {var subQ0=sQuery(id+"F4.wireOp",EDGE,"E12");Q38=makeQuery(id+"F5.opExtrude","SWEPT_FACE",FACE,{"disambiguationData":[OSD([subQ0]),TDD([makeQuery(id+"F4.imprint","IMPRINT",EDGE,{"disambiguationData":[TD([[makeQuery(id+"F4.imprint","INTERSECT",VERTEX,{"derivedFrom":[subQ0,sQuery(id+"F4.wireOp",EDGE,"E21.12.1")]}),-1.0]])],"derivedFrom":subQ0})])]});}
            var Q39;
            {var subQ0=sQuery(id+"F4.wireOp",EDGE,"E12");Q39=makeQuery(id+"F5.opExtrude","SWEPT_FACE",FACE,{"disambiguationData":[OSD([subQ0]),TDD([makeQuery(id+"F4.imprint","IMPRINT",EDGE,{"disambiguationData":[TD([[makeQuery(id+"F4.imprint","INTERSECT",VERTEX,{"derivedFrom":[subQ0,sQuery(id+"F4.wireOp",EDGE,"E21.14.1")]}),-1.0]])],"derivedFrom":subQ0})])]});}
            var Q40;
            {var subQ0=sQuery(id+"F4.wireOp",EDGE,"E12");Q40=makeQuery(id+"F5.opExtrude","SWEPT_FACE",FACE,{"disambiguationData":[OSD([subQ0]),TDD([makeQuery(id+"F4.imprint","IMPRINT",EDGE,{"disambiguationData":[TD([[makeQuery(id+"F4.imprint","INTERSECT",VERTEX,{"derivedFrom":[subQ0,sQuery(id+"F4.wireOp",EDGE,"E21.4.1")]}),-1.0]])],"derivedFrom":subQ0})])]});}
            var Q41;
            {var subQ0=sQuery(id+"F4.wireOp",EDGE,"E12");Q41=makeQuery(id+"F5.opExtrude","SWEPT_FACE",FACE,{"disambiguationData":[OSD([subQ0]),TDD([makeQuery(id+"F4.imprint","IMPRINT",EDGE,{"disambiguationData":[TD([[makeQuery(id+"F4.imprint","INTERSECT",VERTEX,{"derivedFrom":[subQ0,sQuery(id+"F4.wireOp",EDGE,"E21.13.1")]}),-1.0]])],"derivedFrom":subQ0})])]});}
            var Q42;
            {var subQ0=sQuery(id+"F4.wireOp",EDGE,"E12");Q42=makeQuery(id+"F5.opExtrude","SWEPT_FACE",FACE,{"disambiguationData":[OSD([subQ0]),TDD([makeQuery(id+"F4.imprint","IMPRINT",EDGE,{"disambiguationData":[TD([[makeQuery(id+"F4.imprint","INTERSECT",VERTEX,{"derivedFrom":[subQ0,sQuery(id+"F4.wireOp",EDGE,"E20.MirrorCS")]}),1.0]])],"derivedFrom":subQ0})])]});}
            var Q43;
            {var subQ0=sQuery(id+"F4.wireOp",EDGE,"E12");Q43=makeQuery(id+"F5.opExtrude","SWEPT_FACE",FACE,{"disambiguationData":[OSD([subQ0]),TDD([makeQuery(id+"F4.imprint","IMPRINT",EDGE,{"disambiguationData":[TD([[makeQuery(id+"F4.imprint","INTERSECT",VERTEX,{"derivedFrom":[subQ0,sQuery(id+"F4.wireOp",EDGE,"E21.8.1")]}),-1.0]])],"derivedFrom":subQ0})])]});}
            var Q44;
            {var subQ0=sQuery(id+"F4.wireOp",EDGE,"E12");Q44=makeQuery(id+"F5.opExtrude","SWEPT_FACE",FACE,{"disambiguationData":[OSD([subQ0]),TDD([makeQuery(id+"F4.imprint","IMPRINT",EDGE,{"disambiguationData":[TD([[makeQuery(id+"F4.imprint","INTERSECT",VERTEX,{"derivedFrom":[subQ0,sQuery(id+"F4.wireOp",EDGE,"E21.38.1")]}),-1.0]])],"derivedFrom":subQ0})])]});}
            var Q45;
            {var subQ0=sQuery(id+"F4.wireOp",EDGE,"E12");Q45=makeQuery(id+"F5.opExtrude","SWEPT_FACE",FACE,{"disambiguationData":[OSD([subQ0]),TDD([makeQuery(id+"F4.imprint","IMPRINT",EDGE,{"disambiguationData":[TD([[makeQuery(id+"F4.imprint","INTERSECT",VERTEX,{"derivedFrom":[subQ0,sQuery(id+"F4.wireOp",EDGE,"E21.26.1")]}),-1.0]])],"derivedFrom":subQ0})])]});}
            var Q46;
            {var subQ0=sQuery(id+"F4.wireOp",EDGE,"E12");Q46=makeQuery(id+"F5.opExtrude","SWEPT_FACE",FACE,{"disambiguationData":[OSD([subQ0]),TDD([makeQuery(id+"F4.imprint","IMPRINT",EDGE,{"disambiguationData":[TD([[makeQuery(id+"F4.imprint","INTERSECT",VERTEX,{"derivedFrom":[subQ0,sQuery(id+"F4.wireOp",EDGE,"E21.11.1")]}),-1.0]])],"derivedFrom":subQ0})])]});}
            var Q47;
            {var subQ0=sQuery(id+"F4.wireOp",EDGE,"E12");Q47=makeQuery(id+"F5.opExtrude","SWEPT_FACE",FACE,{"disambiguationData":[OSD([subQ0]),TDD([makeQuery(id+"F4.imprint","IMPRINT",EDGE,{"disambiguationData":[TD([[makeQuery(id+"F4.imprint","INTERSECT",VERTEX,{"derivedFrom":[subQ0,sQuery(id+"F4.wireOp",EDGE,"E21.7.1")]}),-1.0]])],"derivedFrom":subQ0})])]});}
            var Q48;
            {var subQ0=sQuery(id+"F4.wireOp",EDGE,"E12");Q48=makeQuery(id+"F5.opExtrude","SWEPT_FACE",FACE,{"disambiguationData":[OSD([subQ0]),TDD([makeQuery(id+"F4.imprint","IMPRINT",EDGE,{"disambiguationData":[TD([[makeQuery(id+"F4.imprint","INTERSECT",VERTEX,{"derivedFrom":[subQ0,sQuery(id+"F4.wireOp",EDGE,"E21.23.1")]}),-1.0]])],"derivedFrom":subQ0})])]});}
            var Q49;
            {var subQ0=sQuery(id+"F4.wireOp",EDGE,"E12");Q49=makeQuery(id+"F5.opExtrude","SWEPT_FACE",FACE,{"disambiguationData":[OSD([subQ0]),TDD([makeQuery(id+"F4.imprint","IMPRINT",EDGE,{"disambiguationData":[TD([[makeQuery(id+"F4.imprint","INTERSECT",VERTEX,{"derivedFrom":[subQ0,sQuery(id+"F4.wireOp",EDGE,"E21.16.1")]}),-1.0]])],"derivedFrom":subQ0})])]});}
            var Q50;
            {var subQ0=sQuery(id+"F4.wireOp",EDGE,"E12");Q50=makeQuery(id+"F5.opExtrude","SWEPT_FACE",FACE,{"disambiguationData":[OSD([subQ0]),TDD([makeQuery(id+"F4.imprint","IMPRINT",EDGE,{"disambiguationData":[TD([[makeQuery(id+"F4.imprint","INTERSECT",VERTEX,{"derivedFrom":[subQ0,sQuery(id+"F4.wireOp",EDGE,"E21.51.1")]}),-1.0]])],"derivedFrom":subQ0})])]});}
            var Q51;
            {var subQ0=sQuery(id+"F4.wireOp",EDGE,"E12");Q51=makeQuery(id+"F5.opExtrude","SWEPT_FACE",FACE,{"disambiguationData":[OSD([subQ0]),TDD([makeQuery(id+"F4.imprint","IMPRINT",EDGE,{"disambiguationData":[TD([[makeQuery(id+"F4.imprint","INTERSECT",VERTEX,{"derivedFrom":[subQ0,sQuery(id+"F4.wireOp",EDGE,"E21.30.1")]}),-1.0]])],"derivedFrom":subQ0})])]});}
            var Q52;
            {var subQ0=sQuery(id+"F4.wireOp",EDGE,"E12");Q52=makeQuery(id+"F5.opExtrude","SWEPT_FACE",FACE,{"disambiguationData":[OSD([subQ0]),TDD([makeQuery(id+"F4.imprint","IMPRINT",EDGE,{"disambiguationData":[TD([[makeQuery(id+"F4.imprint","INTERSECT",VERTEX,{"derivedFrom":[subQ0,sQuery(id+"F4.wireOp",EDGE,"E21.17.1")]}),-1.0]])],"derivedFrom":subQ0})])]});}
            var Q53;
            {var subQ0=sQuery(id+"F4.wireOp",EDGE,"E12");Q53=makeQuery(id+"F5.opExtrude","SWEPT_FACE",FACE,{"disambiguationData":[OSD([subQ0]),TDD([makeQuery(id+"F4.imprint","IMPRINT",EDGE,{"disambiguationData":[TD([[makeQuery(id+"F4.imprint","INTERSECT",VERTEX,{"derivedFrom":[subQ0,sQuery(id+"F4.wireOp",EDGE,"E21.53.1")]}),-1.0]])],"derivedFrom":subQ0})])]});}
            var Q54;
            {var subQ0=sQuery(id+"F4.wireOp",EDGE,"E12");Q54=makeQuery(id+"F5.opExtrude","SWEPT_FACE",FACE,{"disambiguationData":[OSD([subQ0]),TDD([makeQuery(id+"F4.imprint","IMPRINT",EDGE,{"disambiguationData":[TD([[makeQuery(id+"F4.imprint","INTERSECT",VERTEX,{"derivedFrom":[subQ0,sQuery(id+"F4.wireOp",EDGE,"E21.56.1")]}),-1.0]])],"derivedFrom":subQ0})])]});}
            var Q55;
            {var subQ0=sQuery(id+"F4.wireOp",EDGE,"E12");Q55=makeQuery(id+"F5.opExtrude","SWEPT_FACE",FACE,{"disambiguationData":[OSD([subQ0]),TDD([makeQuery(id+"F4.imprint","IMPRINT",EDGE,{"disambiguationData":[TD([[makeQuery(id+"F4.imprint","INTERSECT",VERTEX,{"derivedFrom":[subQ0,sQuery(id+"F4.wireOp",EDGE,"E21.36.1")]}),-1.0]])],"derivedFrom":subQ0})])]});}
            var Q56;
            {var subQ0=sQuery(id+"F4.wireOp",EDGE,"E12");Q56=makeQuery(id+"F5.opExtrude","SWEPT_FACE",FACE,{"disambiguationData":[OSD([subQ0]),TDD([makeQuery(id+"F4.imprint","IMPRINT",EDGE,{"disambiguationData":[TD([[makeQuery(id+"F4.imprint","INTERSECT",VERTEX,{"derivedFrom":[subQ0,sQuery(id+"F4.wireOp",EDGE,"E21.54.1")]}),-1.0]])],"derivedFrom":subQ0})])]});}
            var Q57;
            {var subQ0=sQuery(id+"F4.wireOp",EDGE,"E12");Q57=makeQuery(id+"F5.opExtrude","SWEPT_FACE",FACE,{"disambiguationData":[OSD([subQ0]),TDD([makeQuery(id+"F4.imprint","IMPRINT",EDGE,{"disambiguationData":[TD([[makeQuery(id+"F4.imprint","INTERSECT",VERTEX,{"derivedFrom":[subQ0,sQuery(id+"F4.wireOp",EDGE,"E21.19.1")]}),-1.0]])],"derivedFrom":subQ0})])]});}
            var Q58;
            {var subQ0=sQuery(id+"F4.wireOp",EDGE,"E12");Q58=makeQuery(id+"F5.opExtrude","SWEPT_FACE",FACE,{"disambiguationData":[OSD([subQ0]),TDD([makeQuery(id+"F4.imprint","IMPRINT",EDGE,{"disambiguationData":[TD([[makeQuery(id+"F4.imprint","INTERSECT",VERTEX,{"derivedFrom":[subQ0,sQuery(id+"F4.wireOp",EDGE,"E21.6.1")]}),-1.0]])],"derivedFrom":subQ0})])]});}
            var Q59;
            {var subQ0=sQuery(id+"F4.wireOp",EDGE,"E12");Q59=makeQuery(id+"F5.opExtrude","SWEPT_FACE",FACE,{"disambiguationData":[OSD([subQ0]),TDD([makeQuery(id+"F4.imprint","IMPRINT",EDGE,{"disambiguationData":[TD([[makeQuery(id+"F4.imprint","INTERSECT",VERTEX,{"derivedFrom":[subQ0,sQuery(id+"F4.wireOp",EDGE,"E21.44.1")]}),-1.0]])],"derivedFrom":subQ0})])]});}
            fillet(context, id + "F13", {"entities" : qUnion([Q0, Q1, Q2, Q3, Q4, Q5, Q6, Q7, Q8, Q9, Q10, Q11, Q12, Q13, Q14, Q15, Q16, Q17, Q18, Q19, Q20, Q21, Q22, Q23, Q24, Q25, Q26, Q27, Q28, Q29, Q30, Q31, Q32, Q33, Q34, Q35, Q36, Q37, Q38, Q39, Q40, Q41, Q42, Q43, Q44, Q45, Q46, Q47, Q48, Q49, Q50, Q51, Q52, Q53, Q54, Q55, Q56, Q57, Q58, Q59]), "radius" : 0.3 * mm, "tangentPropagation" : true, "allowEdgeOverflow" : false});
        }
    });
